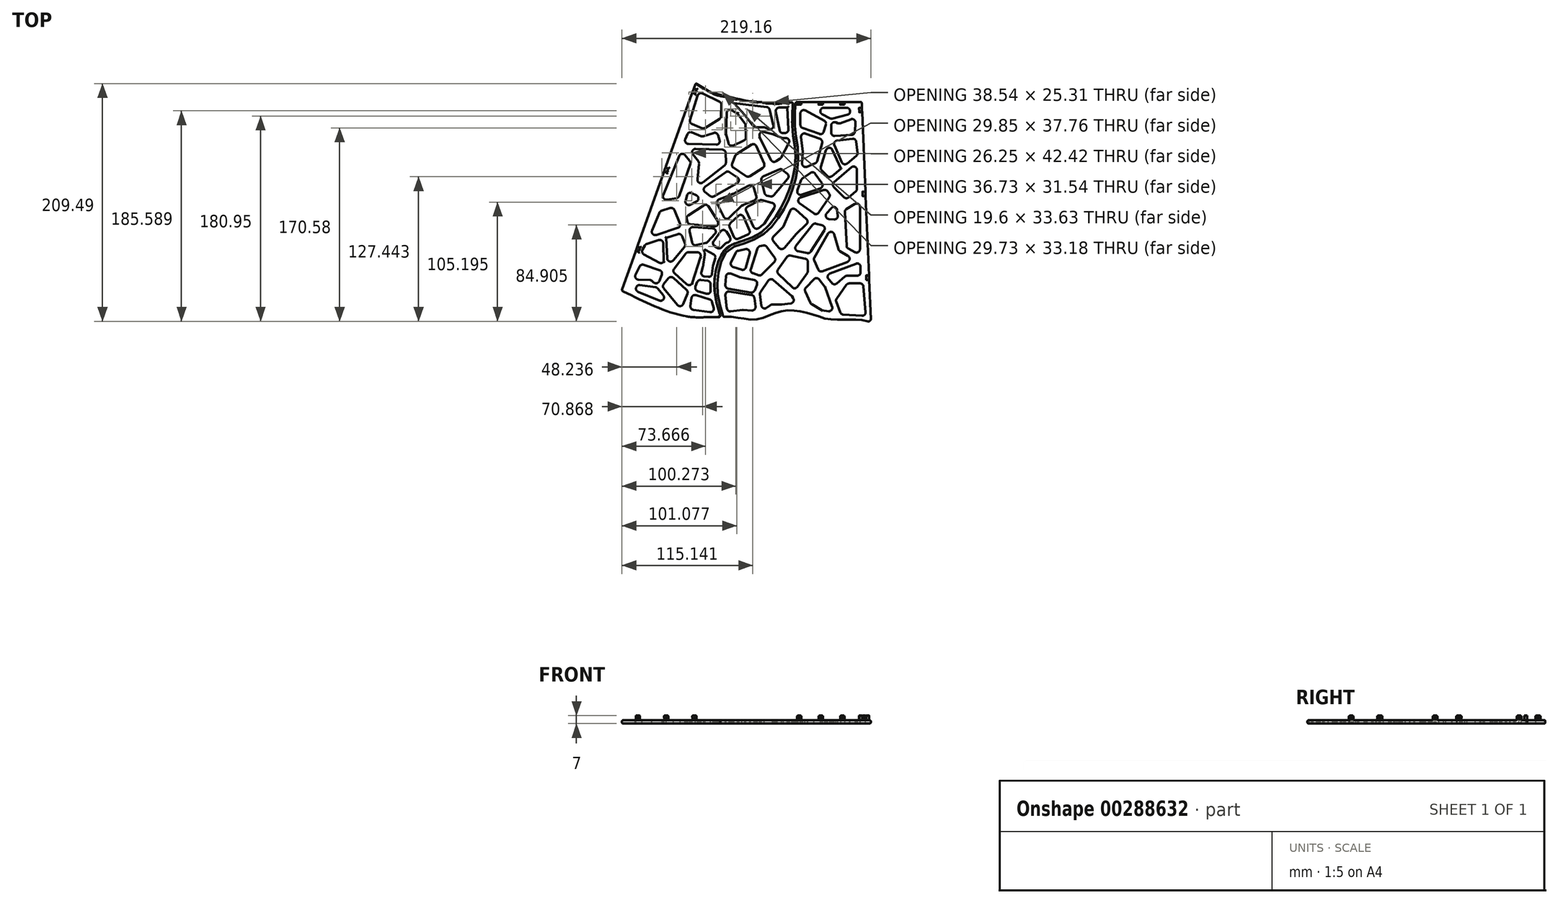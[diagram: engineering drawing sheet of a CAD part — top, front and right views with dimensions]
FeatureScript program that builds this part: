
annotation { "Feature Type Name" : "Feature", "Feature Type Description" : "" }
export const myFeature = defineFeature(function(context is Context, id is Id, definition is map)
    precondition{}
    {
        {
            var Q0;
            Q0=qCreatedBy(makeId("Top.planeOp"),FACE);
            var sketch = newSketch(context, id + "F0", { "sketchPlane" : qUnion([Q0])});
            skPoint(sketch, "E0", {"position": v(69.28, -152.32) * mm});
            skLineSegment(sketch, "E1", {"start": v(30.8, 159.98) * mm, "end": v(38.85, -31.37) * mm});
            skLineSegment(sketch, "E2", {"start": v(30.8, 159.98) * mm, "end": v(-25.68, 159.98) * mm});
            skFitSpline(sketch, "E3", {"points": [v(-27.61, 159.98) * mm, v(-27.61, 133.72) * mm, v(-25.44, 118.63) * mm, v(-27.61, 91.65) * mm, v(-45.45, 53.52) * mm, v(-66.8, 37.33) * mm, v(-86.1, 29.91) * mm, v(-94.25, 14.34) * mm, v(-96.1, -7.92) * mm, v(-91.06, -29.4) * mm], "startDerivative": vector(-8.83, -245.35) * mm, "endDerivative": vector(61.47, -198.5) * mm});
            skFitSpline(sketch, "E4", {"points": [v(-91.06, -29.4) * mm, v(-84.58, -29.4) * mm, v(-69.1, -31.56) * mm, v(-59.54, -31.3) * mm, v(-44.2, -25.79) * mm, v(-29.25, -23.82) * mm, v(-6.17, -29.4) * mm, v(0, -31.34) * mm, v(13.8, -31.87) * mm, v(29.02, -32.13) * mm, v(38.96, -34) * mm], "startDerivative": vector(78.08, 4.89) * mm, "endDerivative": vector(105.84, -25.4) * mm});
            skArc(sketch, "E5.filletArc", {"start": v(-25.68, 159.98) * mm, "mid": v(-27.07, 159.41) * mm, "end": v(-27.68, 158.05) * mm});
            skArc(sketch, "E6.filletArc", {"start": v(-91.52, -27.9) * mm, "mid": v(-90.76, -28.95) * mm, "end": v(-89.52, -29.31) * mm});
            skArc(sketch, "E7.filletArc", {"start": v(36.4, -33.4) * mm, "mid": v(38.13, -32.99) * mm, "end": v(38.85, -31.37) * mm});
            skSolve(sketch);
        }
        {
            var Q0;
            Q0=qCreatedBy(makeId("Top.planeOp"),FACE);
            var sketch = newSketch(context, id + "F1", { "sketchPlane" : qUnion([Q0])});
            skLineSegment(sketch, "E8", {"start": v(-180.19, -4.8) * mm, "end": v(-115.37, 176.62) * mm});
            skFitSpline(sketch, "E9", {"points": [v(-115.37, 176.62) * mm, v(-102.14, 168.68) * mm, v(-86.7, 164.7) * mm, v(-68.18, 160.74) * mm, v(-43.92, 159.41) * mm, v(-29.99, 159.68) * mm], "startDerivative": vector(67.95, -48.1) * mm, "endDerivative": vector(71.48, 2.17) * mm});
            skFitSpline(sketch, "E10", {"points": [v(-29.99, 159.68) * mm, v(-29.99, 155.4) * mm, v(-30.37, 146.31) * mm, v(-29.99, 133.5) * mm, v(-27.85, 118.29) * mm, v(-29.99, 92.6) * mm, v(-47.22, 55.66) * mm, v(-67.43, 39.69) * mm, v(-87.18, 32) * mm, v(-96.99, 14.57) * mm, v(-98.7, -7.72) * mm, v(-93.43, -29.61) * mm], "startDerivative": vector(1.57, -90.12) * mm, "endDerivative": vector(67.23, -218) * mm});
            skFitSpline(sketch, "E11", {"points": [v(-93.43, -29.61) * mm, v(-102.74, -29.61) * mm, v(-119, -29.61) * mm, v(-146.01, -22.4) * mm, v(-168.33, -12.34) * mm, v(-180.8, -6.52) * mm], "startDerivative": vector(-60.72, 1.3) * mm, "endDerivative": vector(-66.19, 30.38) * mm});
            skArc(sketch, "E12.filletArc", {"start": v(-29.96, 157.62) * mm, "mid": v(-30.57, 159.05) * mm, "end": v(-32.02, 159.62) * mm});
            skArc(sketch, "E13.filletArc", {"start": v(-180.19, -4.8) * mm, "mid": v(-180.14, -6.24) * mm, "end": v(-179.14, -7.28) * mm});
            skArc(sketch, "E14.filletArc", {"start": v(-96.18, -29.56) * mm, "mid": v(-94.56, -28.76) * mm, "end": v(-94.24, -26.98) * mm});
            skSolve(sketch);
        }
        {
            var Q0;
            Q0=qCreatedBy(makeId("Top.planeOp"),FACE);
            var sketch = newSketch(context, id + "F2", { "sketchPlane" : qUnion([Q0])});
            skLineSegment(sketch, "E15", {"start": v(31.1, -28.5) * mm, "end": v(14.46, -27.38) * mm});
            skLineSegment(sketch, "E16", {"start": v(11.84, -25.43) * mm, "end": v(8.42, -16.13) * mm});
            skLineSegment(sketch, "E17", {"start": v(8.8, -13.36) * mm, "end": v(17.36, -1.26) * mm});
            skLineSegment(sketch, "E18", {"start": v(19.81, 0) * mm, "end": v(29.41, 0) * mm});
            skLineSegment(sketch, "E19", {"start": v(32.4, -2.75) * mm, "end": v(34.29, -25.26) * mm});
            skLineSegment(sketch, "E20", {"start": v(-1.48, -3.2) * mm, "end": v(4.8, -20.47) * mm});
            skLineSegment(sketch, "E21", {"start": v(1.64, -24.47) * mm, "end": v(-4.13, -23.8) * mm});
            skLineSegment(sketch, "E22", {"start": v(-4.13, -23.8) * mm, "end": v(-13.29, -18.36) * mm});
            skLineSegment(sketch, "E23", {"start": v(-14.5, -17) * mm, "end": v(-18.9, -7.06) * mm});
            skLineSegment(sketch, "E24", {"start": v(-18.35, -3.78) * mm, "end": v(-11.22, 3.75) * mm});
            skLineSegment(sketch, "E25", {"start": v(-6.66, 3.52) * mm, "end": v(-1.48, -3.2) * mm});
            skLineSegment(sketch, "E26", {"start": v(8.78, -0.04) * mm, "end": v(16.2, 6.12) * mm});
            skLineSegment(sketch, "E27", {"start": v(18.13, 6.81) * mm, "end": v(26.87, 6.81) * mm});
            skLineSegment(sketch, "E28", {"start": v(29.87, 9.81) * mm, "end": v(29.87, 14.59) * mm});
            skLineSegment(sketch, "E29", {"start": v(-25.87, -3) * mm, "end": v(-17.08, 9.38) * mm});
            skLineSegment(sketch, "E30", {"start": v(-16.53, 11.12) * mm, "end": v(-16.53, 18.9) * mm});
            skLineSegment(sketch, "E31", {"start": v(-18.93, 21.83) * mm, "end": v(-32.06, 24.49) * mm});
            skLineSegment(sketch, "E32", {"start": v(-35.1, 23.28) * mm, "end": v(-42.92, 12.26) * mm});
            skLineSegment(sketch, "E33", {"start": v(-42.56, 8.37) * mm, "end": v(-30.4, -3.43) * mm});
            skLineSegment(sketch, "E34", {"start": v(-46.96, 3) * mm, "end": v(-30.58, -11.3) * mm});
            skLineSegment(sketch, "E35", {"start": v(-30.58, -11.3) * mm, "end": v(-29.49, -13) * mm});
            skLineSegment(sketch, "E36", {"start": v(-31.66, -17.6) * mm, "end": v(-39.67, -18.53) * mm});
            skLineSegment(sketch, "E37", {"start": v(-39.67, -18.53) * mm, "end": v(-47.78, -18.53) * mm});
            skLineSegment(sketch, "E38", {"start": v(-49.54, -19.1) * mm, "end": v(-52.82, -21.48) * mm});
            skLineSegment(sketch, "E39", {"start": v(-57.56, -19.44) * mm, "end": v(-58.8, -9.65) * mm});
            skLineSegment(sketch, "E40", {"start": v(-58.3, -7.57) * mm, "end": v(-51.4, 2.44) * mm});
            skLineSegment(sketch, "E41", {"start": v(-84.55, -24.65) * mm, "end": v(-74.24, -23.34) * mm});
            skLineSegment(sketch, "E42", {"start": v(-73.65, -23.32) * mm, "end": v(-65.92, -23.84) * mm});
            skLineSegment(sketch, "E43", {"start": v(-62.74, -20.46) * mm, "end": v(-63.73, -12.76) * mm});
            skLineSegment(sketch, "E44", {"start": v(-63.4, -6.1) * mm, "end": v(-61.43, -1.08) * mm});
            skLineSegment(sketch, "E45", {"start": v(-63.63, 2.95) * mm, "end": v(-76.87, 5.63) * mm});
            skLineSegment(sketch, "E46", {"start": v(-77.37, 5.78) * mm, "end": v(-84.68, 8.66) * mm});
            skLineSegment(sketch, "E47", {"start": v(-88.77, 6.07) * mm, "end": v(-89.28, -1.4) * mm});
            skLineSegment(sketch, "E48", {"start": v(-89.2, -10.44) * mm, "end": v(-87.9, -22) * mm});
            skLineSegment(sketch, "E49", {"start": v(-80.06, 27.24) * mm, "end": v(-84.2, 18.7) * mm});
            skLineSegment(sketch, "E50", {"start": v(-82.43, 14.54) * mm, "end": v(-74.91, 12.12) * mm});
            skLineSegment(sketch, "E51", {"start": v(-56.79, 8.03) * mm, "end": v(-46.16, 18.98) * mm});
            skLineSegment(sketch, "E52", {"start": v(-45.89, 22.83) * mm, "end": v(-52.69, 32.18) * mm});
            skLineSegment(sketch, "E53", {"start": v(-55.7, 33.36) * mm, "end": v(-58.78, 32.74) * mm});
            skLineSegment(sketch, "E54", {"start": v(-47, 37.37) * mm, "end": v(-41.99, 31.34) * mm});
            skLineSegment(sketch, "E55", {"start": v(-37.39, 31.32) * mm, "end": v(-26.9, 43.75) * mm});
            skLineSegment(sketch, "E56", {"start": v(-26.9, 43.75) * mm, "end": v(-17.78, 52.23) * mm});
            skLineSegment(sketch, "E57", {"start": v(-17.84, 56.69) * mm, "end": v(-27.46, 65.12) * mm});
            skLineSegment(sketch, "E58", {"start": v(-32.2, 64.04) * mm, "end": v(-38.22, 49.87) * mm});
            skLineSegment(sketch, "E59", {"start": v(-38.22, 49.87) * mm, "end": v(-46.8, 41.42) * mm});
            skLineSegment(sketch, "E60", {"start": v(15.95, 62.82) * mm, "end": v(17.52, 33.04) * mm});
            skLineSegment(sketch, "E61", {"start": v(19.15, 30.53) * mm, "end": v(24.94, 27.57) * mm});
            skLineSegment(sketch, "E62", {"start": v(29.3, 30.24) * mm, "end": v(29.3, 49.62) * mm});
            skLineSegment(sketch, "E63", {"start": v(29.3, 49.62) * mm, "end": v(29.3, 67.45) * mm});
            skLineSegment(sketch, "E64", {"start": v(24.75, 70.01) * mm, "end": v(17.39, 65.55) * mm});
            skLineSegment(sketch, "E65", {"start": v(-23.8, 70.53) * mm, "end": v(-11.29, 61.65) * mm});
            skLineSegment(sketch, "E66", {"start": v(-7.08, 62.4) * mm, "end": v(2.16, 75.8) * mm});
            skLineSegment(sketch, "E67", {"start": v(2.15, 79.23) * mm, "end": v(0.82, 81.12) * mm});
            skLineSegment(sketch, "E68", {"start": v(-14.33, 97.44) * mm, "end": v(-21.45, 92.43) * mm});
            skLineSegment(sketch, "E69", {"start": v(-22.54, 91) * mm, "end": v(-25.8, 82.09) * mm});
            skLineSegment(sketch, "E70", {"start": v(4, 66.34) * mm, "end": v(-0.04, 61.73) * mm});
            skLineSegment(sketch, "E71", {"start": v(2.01, 56.76) * mm, "end": v(6.66, 56.45) * mm});
            skLineSegment(sketch, "E72", {"start": v(9.84, 59.8) * mm, "end": v(9.23, 64.73) * mm});
            skLineSegment(sketch, "E73", {"start": v(6.25, 85.01) * mm, "end": v(15.14, 75.99) * mm});
            skLineSegment(sketch, "E74", {"start": v(19.19, 75.79) * mm, "end": v(25.57, 81.08) * mm});
            skLineSegment(sketch, "E75", {"start": v(26.65, 83.4) * mm, "end": v(26.65, 100.03) * mm});
            skLineSegment(sketch, "E76", {"start": v(21.71, 102.33) * mm, "end": v(6.44, 89.4) * mm});
            skLineSegment(sketch, "E77", {"start": v(-4.47, 99.7) * mm, "end": v(0.44, 94.73) * mm});
            skLineSegment(sketch, "E78", {"start": v(4.5, 94.53) * mm, "end": v(12.58, 101.24) * mm});
            skLineSegment(sketch, "E79", {"start": v(27.22, 115.21) * mm, "end": v(25.98, 124.95) * mm});
            skLineSegment(sketch, "E80", {"start": v(22.62, 127.54) * mm, "end": v(9.09, 125.81) * mm});
            skLineSegment(sketch, "E81", {"start": v(-0.62, 117.4) * mm, "end": v(-5.2, 102.7) * mm});
            skLineSegment(sketch, "E82", {"start": v(-22.57, 128.81) * mm, "end": v(-20.98, 116.36) * mm});
            skLineSegment(sketch, "E83", {"start": v(-20.96, 115.77) * mm, "end": v(-21.63, 105.8) * mm});
            skLineSegment(sketch, "E84", {"start": v(-17.5, 102.83) * mm, "end": v(-10.17, 105.86) * mm});
            skLineSegment(sketch, "E85", {"start": v(-8.42, 107.85) * mm, "end": v(-4.07, 123.93) * mm});
            skLineSegment(sketch, "E86", {"start": v(-5.97, 127.54) * mm, "end": v(-18.6, 132.02) * mm});
            skLineSegment(sketch, "E87", {"start": v(-23.2, 149.78) * mm, "end": v(-23.2, 139.85) * mm});
            skLineSegment(sketch, "E88", {"start": v(-21.2, 137.02) * mm, "end": v(-6.46, 131.76) * mm});
            skLineSegment(sketch, "E89", {"start": v(-2.58, 133.72) * mm, "end": v(-0.7, 139.93) * mm});
            skLineSegment(sketch, "E90", {"start": v(-2.15, 143.44) * mm, "end": v(-18.77, 152.42) * mm});
            skLineSegment(sketch, "E91", {"start": v(-4.02, 149.16) * mm, "end": v(2.88, 145.52) * mm});
            skLineSegment(sketch, "E92", {"start": v(5, 145.26) * mm, "end": v(18.36, 148.6) * mm});
            skLineSegment(sketch, "E93", {"start": v(20.61, 151.9) * mm, "end": v(20.57, 152.2) * mm});
            skLineSegment(sketch, "E94", {"start": v(17.6, 154.81) * mm, "end": v(-2.62, 154.81) * mm});
            skLineSegment(sketch, "E95", {"start": v(3.97, 139.12) * mm, "end": v(3.97, 132.96) * mm});
            skLineSegment(sketch, "E96", {"start": v(7.16, 129.96) * mm, "end": v(22.02, 130.9) * mm});
            skLineSegment(sketch, "E97", {"start": v(24.83, 133.69) * mm, "end": v(25.37, 141.7) * mm});
            skLineSegment(sketch, "E98", {"start": v(21.35, 144.72) * mm, "end": v(11.84, 141.26) * mm});
            skLineSegment(sketch, "E99", {"start": v(9.74, 141.27) * mm, "end": v(8.05, 141.92) * mm});
            skLineSegment(sketch, "E100", {"start": v(4.56, 0.35) * mm, "end": v(1.57, 3.94) * mm});
            skLineSegment(sketch, "E101", {"start": v(2.81, 8.67) * mm, "end": v(25.8, 17.4) * mm});
            skLineSegment(sketch, "E102", {"start": v(1.16, 43.91) * mm, "end": v(-10.86, 22.74) * mm});
            skLineSegment(sketch, "E103", {"start": v(-11, 20.04) * mm, "end": v(-7.57, 12.33) * mm});
            skLineSegment(sketch, "E104", {"start": v(-3.77, 10.74) * mm, "end": v(18.23, 19) * mm});
            skLineSegment(sketch, "E105", {"start": v(18.67, 24.41) * mm, "end": v(11.7, 28.42) * mm});
            skLineSegment(sketch, "E106", {"start": v(10.31, 30.2) * mm, "end": v(6.65, 43.24) * mm});
            skLineSegment(sketch, "E107", {"start": v(-12.4, 51.63) * mm, "end": v(-27.02, 33.16) * mm});
            skLineSegment(sketch, "E108", {"start": v(-25.26, 28.36) * mm, "end": v(-17.12, 26.7) * mm});
            skLineSegment(sketch, "E109", {"start": v(-13.99, 28.05) * mm, "end": v(-2.17, 46.73) * mm});
            skLineSegment(sketch, "E110", {"start": v(-3.93, 51.23) * mm, "end": v(-9.27, 52.67) * mm});
            skLineSegment(sketch, "E111", {"start": v(4.97, 117.77) * mm, "end": v(12.58, 101.24) * mm});
            skPoint(sketch, "E112.endSnap0", {"position": v(14.9, 103.17) * mm});
            skLineSegment(sketch, "E113.trimOffspring", {"start": v(17.96, 105.7) * mm, "end": v(26.17, 112.52) * mm});
            skLineSegment(sketch, "E114", {"start": v(-22.02, 78.21) * mm, "end": v(-5.71, 83.71) * mm});
            skLineSegment(sketch, "E115", {"start": v(-22.97, 75.84) * mm, "end": v(-2.53, 82.25) * mm});
            skLineSegment(sketch, "E116.trimOffspring", {"start": v(-4.22, 88.28) * mm, "end": v(-10.15, 96.71) * mm});
            skLineSegment(sketch, "E117", {"start": v(-71.1, 14.2) * mm, "end": v(-67.85, 26.5) * mm});
            skLineSegment(sketch, "E118", {"start": v(-66.86, 12.67) * mm, "end": v(-61.04, 30.72) * mm});
            skLineSegment(sketch, "E119", {"start": v(-66.7, -7.97) * mm, "end": v(-86.79, -4.56) * mm});
            skLineSegment(sketch, "E120", {"start": v(-85.75, -7.14) * mm, "end": v(-66.24, -10.17) * mm});
            skLineSegment(sketch, "E121.trimOffspring", {"start": v(-64.92, 8.9) * mm, "end": v(-59.86, 7.27) * mm});
            skLineSegment(sketch, "E122.trimOffspring", {"start": v(-71.34, 30.2) * mm, "end": v(-77.96, 28.87) * mm});
            skPoint(sketch, "E123.visualSharp", {"position": v(-23.2, 154.81) * mm});
            skArc(sketch, "E123.filletArc", {"start": v(-18.77, 152.42) * mm, "mid": v(-21.73, 152.36) * mm, "end": v(-23.2, 149.78) * mm});
            skPoint(sketch, "E124.visualSharp", {"position": v(-14.73, 154.81) * mm});
            skArc(sketch, "E124.filletArc", {"start": v(-2.62, 154.81) * mm, "mid": v(-5.53, 152.53) * mm, "end": v(-4.02, 149.16) * mm});
            skPoint(sketch, "E125.visualSharp", {"position": v(20.24, 154.81) * mm});
            skArc(sketch, "E125.filletArc", {"start": v(20.57, 152.2) * mm, "mid": v(19.58, 154.06) * mm, "end": v(17.6, 154.81) * mm});
            skPoint(sketch, "E126.visualSharp", {"position": v(20.95, 149.25) * mm});
            skArc(sketch, "E126.filletArc", {"start": v(18.36, 148.6) * mm, "mid": v(20.11, 149.82) * mm, "end": v(20.61, 151.9) * mm});
            skPoint(sketch, "E127.visualSharp", {"position": v(3.9, 144.98) * mm});
            skArc(sketch, "E127.filletArc", {"start": v(2.88, 145.52) * mm, "mid": v(3.92, 145.2) * mm, "end": v(5, 145.26) * mm});
            skPoint(sketch, "E128.visualSharp", {"position": v(3.97, 143.48) * mm});
            skArc(sketch, "E128.filletArc", {"start": v(8.05, 141.92) * mm, "mid": v(5.27, 141.6) * mm, "end": v(3.97, 139.12) * mm});
            skPoint(sketch, "E129.visualSharp", {"position": v(25.68, 146.3) * mm});
            skArc(sketch, "E129.filletArc", {"start": v(25.37, 141.7) * mm, "mid": v(24.18, 144.3) * mm, "end": v(21.35, 144.72) * mm});
            skPoint(sketch, "E130.visualSharp", {"position": v(10.78, 140.87) * mm});
            skArc(sketch, "E130.filletArc", {"start": v(9.74, 141.27) * mm, "mid": v(10.79, 141.07) * mm, "end": v(11.84, 141.26) * mm});
            skPoint(sketch, "E131.visualSharp", {"position": v(3.97, 129.76) * mm});
            skArc(sketch, "E131.filletArc", {"start": v(3.97, 132.96) * mm, "mid": v(4.92, 130.77) * mm, "end": v(7.16, 129.96) * mm});
            skPoint(sketch, "E132.visualSharp", {"position": v(24.65, 131.06) * mm});
            skArc(sketch, "E132.filletArc", {"start": v(22.02, 130.9) * mm, "mid": v(23.95, 131.76) * mm, "end": v(24.83, 133.69) * mm});
            skPoint(sketch, "E133.visualSharp", {"position": v(25.6, 127.92) * mm});
            skArc(sketch, "E133.filletArc", {"start": v(25.98, 124.95) * mm, "mid": v(24.84, 126.94) * mm, "end": v(22.62, 127.54) * mm});
            skPoint(sketch, "E134.visualSharp", {"position": v(5.1, 125.3) * mm});
            skArc(sketch, "E134.filletArc", {"start": v(9.09, 125.81) * mm, "mid": v(6.86, 124.3) * mm, "end": v(6.73, 121.62) * mm});
            skPoint(sketch, "E135.visualSharp", {"position": v(27.43, 113.58) * mm});
            skArc(sketch, "E135.filletArc", {"start": v(26.17, 112.52) * mm, "mid": v(27.04, 113.73) * mm, "end": v(27.22, 115.21) * mm});
            skPoint(sketch, "E136.visualSharp", {"position": v(26.65, 106.5) * mm});
            skArc(sketch, "E136.filletArc", {"start": v(26.65, 100.03) * mm, "mid": v(24.91, 102.76) * mm, "end": v(21.71, 102.33) * mm});
            skPoint(sketch, "E137.visualSharp", {"position": v(17.07, 74.02) * mm});
            skArc(sketch, "E137.filletArc", {"start": v(15.14, 75.99) * mm, "mid": v(17.12, 75.1) * mm, "end": v(19.19, 75.79) * mm});
            skPoint(sketch, "E138.visualSharp", {"position": v(26.65, 81.98) * mm});
            skArc(sketch, "E138.filletArc", {"start": v(25.57, 81.08) * mm, "mid": v(26.37, 82.12) * mm, "end": v(26.65, 83.4) * mm});
            skPoint(sketch, "E139.visualSharp", {"position": v(3.97, 87.32) * mm});
            skArc(sketch, "E139.filletArc", {"start": v(6.44, 89.4) * mm, "mid": v(5.39, 87.25) * mm, "end": v(6.25, 85.01) * mm});
            skPoint(sketch, "E140.visualSharp", {"position": v(2.37, 92.76) * mm});
            skArc(sketch, "E140.filletArc", {"start": v(0.44, 94.73) * mm, "mid": v(2.43, 93.84) * mm, "end": v(4.5, 94.53) * mm});
            skPoint(sketch, "E141.visualSharp", {"position": v(-5.73, 100.99) * mm});
            skArc(sketch, "E141.filletArc", {"start": v(-5.2, 102.7) * mm, "mid": v(-5.25, 101.1) * mm, "end": v(-4.47, 99.7) * mm});
            skPoint(sketch, "E142.visualSharp", {"position": v(-3.35, 126.6) * mm});
            skArc(sketch, "E142.filletArc", {"start": v(-4.07, 123.93) * mm, "mid": v(-4.31, 126.1) * mm, "end": v(-5.97, 127.54) * mm});
            skPoint(sketch, "E143.visualSharp", {"position": v(-8.8, 106.42) * mm});
            skArc(sketch, "E143.filletArc", {"start": v(-10.17, 105.86) * mm, "mid": v(-9.06, 106.65) * mm, "end": v(-8.42, 107.85) * mm});
            skPoint(sketch, "E144.visualSharp", {"position": v(-23.2, 133.66) * mm});
            skArc(sketch, "E144.filletArc", {"start": v(-18.6, 132.02) * mm, "mid": v(-21.48, 131.53) * mm, "end": v(-22.57, 128.81) * mm});
            skPoint(sketch, "E145.visualSharp", {"position": v(-21.96, 100.99) * mm});
            skArc(sketch, "E145.filletArc", {"start": v(-21.63, 105.8) * mm, "mid": v(-20.4, 103.17) * mm, "end": v(-17.5, 102.83) * mm});
            skPoint(sketch, "E146.visualSharp", {"position": v(-20.94, 116.07) * mm});
            skArc(sketch, "E146.filletArc", {"start": v(-20.96, 115.77) * mm, "mid": v(-20.96, 116.06) * mm, "end": v(-20.98, 116.36) * mm});
            skPoint(sketch, "E147.visualSharp", {"position": v(-11.87, 99.17) * mm});
            skArc(sketch, "E147.filletArc", {"start": v(-10.15, 96.71) * mm, "mid": v(-12.08, 97.94) * mm, "end": v(-14.33, 97.44) * mm});
            skPoint(sketch, "E148.visualSharp", {"position": v(-27.94, 76.22) * mm});
            skArc(sketch, "E148.filletArc", {"start": v(-25.8, 82.09) * mm, "mid": v(-25.13, 78.96) * mm, "end": v(-22.02, 78.21) * mm});
            skPoint(sketch, "E149.visualSharp", {"position": v(-1.91, 85) * mm});
            skArc(sketch, "E149.filletArc", {"start": v(-5.71, 83.71) * mm, "mid": v(-3.82, 85.62) * mm, "end": v(-4.22, 88.28) * mm});
            skPoint(sketch, "E150.visualSharp", {"position": v(-22.22, 91.9) * mm});
            skArc(sketch, "E150.filletArc", {"start": v(-21.45, 92.43) * mm, "mid": v(-22.1, 91.8) * mm, "end": v(-22.54, 91) * mm});
            skPoint(sketch, "E151.visualSharp", {"position": v(-0.44, 82.91) * mm});
            skArc(sketch, "E151.filletArc", {"start": v(0.82, 81.12) * mm, "mid": v(-0.67, 82.23) * mm, "end": v(-2.53, 82.25) * mm});
            skPoint(sketch, "E152.visualSharp", {"position": v(3.35, 77.52) * mm});
            skArc(sketch, "E152.filletArc", {"start": v(2.16, 75.8) * mm, "mid": v(2.7, 77.52) * mm, "end": v(2.15, 79.23) * mm});
            skPoint(sketch, "E153.visualSharp", {"position": v(-8.8, 59.89) * mm});
            skArc(sketch, "E153.filletArc", {"start": v(-11.29, 61.65) * mm, "mid": v(-9.03, 61.14) * mm, "end": v(-7.08, 62.4) * mm});
            skPoint(sketch, "E154.visualSharp", {"position": v(-4.05, 57.17) * mm});
            skArc(sketch, "E154.filletArc", {"start": v(-0.04, 61.73) * mm, "mid": v(-0.56, 58.6) * mm, "end": v(2.01, 56.76) * mm});
            skPoint(sketch, "E155.visualSharp", {"position": v(10.28, 56.2) * mm});
            skArc(sketch, "E155.filletArc", {"start": v(6.66, 56.45) * mm, "mid": v(9.04, 57.38) * mm, "end": v(9.84, 59.8) * mm});
            skPoint(sketch, "E156.visualSharp", {"position": v(-28.74, 74.02) * mm});
            skArc(sketch, "E156.filletArc", {"start": v(-22.97, 75.84) * mm, "mid": v(-25.04, 73.44) * mm, "end": v(-23.8, 70.53) * mm});
            skPoint(sketch, "E157.visualSharp", {"position": v(8.41, 71.38) * mm});
            skArc(sketch, "E157.filletArc", {"start": v(9.23, 64.73) * mm, "mid": v(7.14, 67.23) * mm, "end": v(4, 66.34) * mm});
            skPoint(sketch, "E158.visualSharp", {"position": v(15.85, 64.62) * mm});
            skArc(sketch, "E158.filletArc", {"start": v(17.39, 65.55) * mm, "mid": v(16.29, 64.38) * mm, "end": v(15.95, 62.82) * mm});
            skPoint(sketch, "E159.visualSharp", {"position": v(29.3, 72.78) * mm});
            skArc(sketch, "E159.filletArc", {"start": v(29.3, 67.45) * mm, "mid": v(27.78, 70.06) * mm, "end": v(24.75, 70.01) * mm});
            skPoint(sketch, "E160.visualSharp", {"position": v(17.62, 31.32) * mm});
            skArc(sketch, "E160.filletArc", {"start": v(17.52, 33.04) * mm, "mid": v(18, 31.57) * mm, "end": v(19.15, 30.53) * mm});
            skPoint(sketch, "E161.visualSharp", {"position": v(29.3, 25.33) * mm});
            skArc(sketch, "E161.filletArc", {"start": v(24.94, 27.57) * mm, "mid": v(27.87, 27.68) * mm, "end": v(29.3, 30.24) * mm});
            skPoint(sketch, "E162.visualSharp", {"position": v(-1.11, 7.18) * mm});
            skArc(sketch, "E162.filletArc", {"start": v(2.81, 8.67) * mm, "mid": v(0.98, 6.63) * mm, "end": v(1.57, 3.94) * mm});
            skPoint(sketch, "E163.visualSharp", {"position": v(6.48, -1.96) * mm});
            skArc(sketch, "E163.filletArc", {"start": v(4.56, 0.35) * mm, "mid": v(6.6, -0.72) * mm, "end": v(8.78, -0.04) * mm});
            skPoint(sketch, "E164.visualSharp", {"position": v(29.87, 18.93) * mm});
            skArc(sketch, "E164.filletArc", {"start": v(29.87, 14.59) * mm, "mid": v(28.57, 17.06) * mm, "end": v(25.8, 17.4) * mm});
            skPoint(sketch, "E165.visualSharp", {"position": v(17.04, 6.81) * mm});
            skArc(sketch, "E165.filletArc", {"start": v(18.13, 6.81) * mm, "mid": v(17.1, 6.64) * mm, "end": v(16.2, 6.12) * mm});
            skPoint(sketch, "E166.visualSharp", {"position": v(29.87, 6.81) * mm});
            skArc(sketch, "E166.filletArc", {"start": v(26.87, 6.81) * mm, "mid": v(28.99, 7.7) * mm, "end": v(29.87, 9.81) * mm});
            skPoint(sketch, "E167.visualSharp", {"position": v(24.18, 21.24) * mm});
            skArc(sketch, "E167.filletArc", {"start": v(18.23, 19) * mm, "mid": v(20.16, 21.57) * mm, "end": v(18.67, 24.41) * mm});
            skPoint(sketch, "E168.visualSharp", {"position": v(4.7, 50.17) * mm});
            skArc(sketch, "E168.filletArc", {"start": v(6.65, 43.24) * mm, "mid": v(4.13, 45.4) * mm, "end": v(1.16, 43.91) * mm});
            skPoint(sketch, "E169.visualSharp", {"position": v(-11.61, 21.42) * mm});
            skArc(sketch, "E169.filletArc", {"start": v(-10.86, 22.74) * mm, "mid": v(-11.25, 21.4) * mm, "end": v(-11, 20.04) * mm});
            skPoint(sketch, "E170.visualSharp", {"position": v(10.64, 29.03) * mm});
            skArc(sketch, "E170.filletArc", {"start": v(10.31, 30.2) * mm, "mid": v(10.83, 29.18) * mm, "end": v(11.7, 28.42) * mm});
            skPoint(sketch, "E171.visualSharp", {"position": v(-8.8, 6.3) * mm});
            skArc(sketch, "E171.filletArc", {"start": v(-6.66, 3.52) * mm, "mid": v(-8.89, 4.69) * mm, "end": v(-11.22, 3.75) * mm});
            skPoint(sketch, "E172.visualSharp", {"position": v(6.48, -25.04) * mm});
            skArc(sketch, "E172.filletArc", {"start": v(1.64, -24.47) * mm, "mid": v(4.34, -23.35) * mm, "end": v(4.8, -20.47) * mm});
            skPoint(sketch, "E173.visualSharp", {"position": v(-19.72, -5.24) * mm});
            skArc(sketch, "E173.filletArc", {"start": v(-18.35, -3.78) * mm, "mid": v(-19.13, -5.34) * mm, "end": v(-18.9, -7.06) * mm});
            skPoint(sketch, "E174.visualSharp", {"position": v(7.88, -14.64) * mm});
            skArc(sketch, "E174.filletArc", {"start": v(8.8, -13.36) * mm, "mid": v(8.26, -14.7) * mm, "end": v(8.42, -16.13) * mm});
            skPoint(sketch, "E175.visualSharp", {"position": v(18.26, 0) * mm});
            skArc(sketch, "E175.filletArc", {"start": v(19.81, 0) * mm, "mid": v(18.43, -0.33) * mm, "end": v(17.36, -1.26) * mm});
            skPoint(sketch, "E176.visualSharp", {"position": v(32.17, 0) * mm});
            skArc(sketch, "E176.filletArc", {"start": v(32.4, -2.75) * mm, "mid": v(31.44, -0.8) * mm, "end": v(29.41, 0) * mm});
            skPoint(sketch, "E177.visualSharp", {"position": v(34.58, -28.74) * mm});
            skArc(sketch, "E177.filletArc", {"start": v(31.1, -28.5) * mm, "mid": v(33.44, -27.61) * mm, "end": v(34.29, -25.26) * mm});
            skPoint(sketch, "E178.visualSharp", {"position": v(12.51, -27.25) * mm});
            skArc(sketch, "E178.filletArc", {"start": v(11.84, -25.43) * mm, "mid": v(12.86, -26.8) * mm, "end": v(14.46, -27.38) * mm});
            skPoint(sketch, "E179.visualSharp", {"position": v(-26.87, -17.04) * mm});
            skArc(sketch, "E179.filletArc", {"start": v(-31.66, -17.6) * mm, "mid": v(-29.3, -15.9) * mm, "end": v(-29.49, -13) * mm});
            skPoint(sketch, "E180.visualSharp", {"position": v(-58.95, -8.51) * mm});
            skArc(sketch, "E180.filletArc", {"start": v(-58.3, -7.57) * mm, "mid": v(-58.75, -8.56) * mm, "end": v(-58.8, -9.65) * mm});
            skPoint(sketch, "E181.visualSharp", {"position": v(-49.5, 5.2) * mm});
            skArc(sketch, "E181.filletArc", {"start": v(-46.96, 3) * mm, "mid": v(-49.3, 3.71) * mm, "end": v(-51.4, 2.44) * mm});
            skPoint(sketch, "E182.visualSharp", {"position": v(-48.75, -18.53) * mm});
            skArc(sketch, "E182.filletArc", {"start": v(-47.78, -18.53) * mm, "mid": v(-48.7, -18.68) * mm, "end": v(-49.54, -19.1) * mm});
            skPoint(sketch, "E183.visualSharp", {"position": v(-56.91, -24.46) * mm});
            skArc(sketch, "E183.filletArc", {"start": v(-57.56, -19.44) * mm, "mid": v(-55.77, -21.81) * mm, "end": v(-52.82, -21.48) * mm});
            skPoint(sketch, "E184.visualSharp", {"position": v(-62.28, -24.08) * mm});
            skArc(sketch, "E184.filletArc", {"start": v(-65.92, -23.84) * mm, "mid": v(-63.53, -22.9) * mm, "end": v(-62.74, -20.46) * mm});
            skPoint(sketch, "E185.visualSharp", {"position": v(-87.57, -25.04) * mm});
            skArc(sketch, "E185.filletArc", {"start": v(-87.9, -22) * mm, "mid": v(-86.78, -24.04) * mm, "end": v(-84.55, -24.65) * mm});
            skPoint(sketch, "E186.visualSharp", {"position": v(-64.01, -10.52) * mm});
            skArc(sketch, "E186.filletArc", {"start": v(-63.73, -12.76) * mm, "mid": v(-64.55, -11.04) * mm, "end": v(-66.24, -10.17) * mm});
            skPoint(sketch, "E187.visualSharp", {"position": v(-64.28, -8.38) * mm});
            skArc(sketch, "E187.filletArc", {"start": v(-66.7, -7.97) * mm, "mid": v(-64.71, -7.63) * mm, "end": v(-63.4, -6.1) * mm});
            skPoint(sketch, "E188.visualSharp", {"position": v(-89.46, -4.1) * mm});
            skArc(sketch, "E188.filletArc", {"start": v(-89.28, -1.4) * mm, "mid": v(-88.64, -3.46) * mm, "end": v(-86.79, -4.56) * mm});
            skPoint(sketch, "E189.visualSharp", {"position": v(-85.72, 15.6) * mm});
            skArc(sketch, "E189.filletArc", {"start": v(-84.2, 18.7) * mm, "mid": v(-84.27, 16.22) * mm, "end": v(-82.43, 14.54) * mm});
            skPoint(sketch, "E190.visualSharp", {"position": v(-66.62, 31.16) * mm});
            skArc(sketch, "E190.filletArc", {"start": v(-67.85, 26.5) * mm, "mid": v(-68.56, 29.32) * mm, "end": v(-71.34, 30.2) * mm});
            skPoint(sketch, "E191.visualSharp", {"position": v(-88.5, 10.16) * mm});
            skArc(sketch, "E191.filletArc", {"start": v(-84.68, 8.66) * mm, "mid": v(-87.39, 8.4) * mm, "end": v(-88.77, 6.07) * mm});
            skPoint(sketch, "E192.visualSharp", {"position": v(-71.9, 11.15) * mm});
            skArc(sketch, "E192.filletArc", {"start": v(-74.91, 12.12) * mm, "mid": v(-72.56, 12.34) * mm, "end": v(-71.1, 14.2) * mm});
            skPoint(sketch, "E193.visualSharp", {"position": v(-79.41, 28.58) * mm});
            skArc(sketch, "E193.filletArc", {"start": v(-77.96, 28.87) * mm, "mid": v(-79.2, 28.3) * mm, "end": v(-80.06, 27.24) * mm});
            skPoint(sketch, "E194.visualSharp", {"position": v(-60.5, 32.4) * mm});
            skArc(sketch, "E194.filletArc", {"start": v(-58.78, 32.74) * mm, "mid": v(-60.19, 32.04) * mm, "end": v(-61.04, 30.72) * mm});
            skPoint(sketch, "E195.visualSharp", {"position": v(-53.82, 33.74) * mm});
            skArc(sketch, "E195.filletArc", {"start": v(-52.69, 32.18) * mm, "mid": v(-54.03, 33.21) * mm, "end": v(-55.7, 33.36) * mm});
            skPoint(sketch, "E196.visualSharp", {"position": v(-44.4, 20.8) * mm});
            skArc(sketch, "E196.filletArc", {"start": v(-46.16, 18.98) * mm, "mid": v(-45.32, 20.86) * mm, "end": v(-45.89, 22.83) * mm});
            skPoint(sketch, "E197.visualSharp", {"position": v(-67.78, 9.82) * mm});
            skArc(sketch, "E197.filletArc", {"start": v(-66.86, 12.67) * mm, "mid": v(-66.67, 10.39) * mm, "end": v(-64.92, 8.9) * mm});
            skPoint(sketch, "E198.visualSharp", {"position": v(-58.09, 6.7) * mm});
            skArc(sketch, "E198.filletArc", {"start": v(-59.86, 7.27) * mm, "mid": v(-58.22, 7.21) * mm, "end": v(-56.79, 8.03) * mm});
            skPoint(sketch, "E199.visualSharp", {"position": v(-33.97, 24.88) * mm});
            skArc(sketch, "E199.filletArc", {"start": v(-32.06, 24.49) * mm, "mid": v(-33.76, 24.34) * mm, "end": v(-35.1, 23.28) * mm});
            skPoint(sketch, "E200.visualSharp", {"position": v(-16.53, 21.35) * mm});
            skArc(sketch, "E200.filletArc", {"start": v(-16.53, 18.9) * mm, "mid": v(-17.2, 20.8) * mm, "end": v(-18.93, 21.83) * mm});
            skPoint(sketch, "E201.visualSharp", {"position": v(-16.53, 10.16) * mm});
            skArc(sketch, "E201.filletArc", {"start": v(-17.08, 9.38) * mm, "mid": v(-16.67, 10.2) * mm, "end": v(-16.53, 11.12) * mm});
            skPoint(sketch, "E202.visualSharp", {"position": v(-27.9, -5.86) * mm});
            skArc(sketch, "E202.filletArc", {"start": v(-30.4, -3.43) * mm, "mid": v(-28.04, -4.26) * mm, "end": v(-25.87, -3) * mm});
            skPoint(sketch, "E203.visualSharp", {"position": v(-44.4, 10.16) * mm});
            skArc(sketch, "E203.filletArc", {"start": v(-42.92, 12.26) * mm, "mid": v(-43.46, 10.25) * mm, "end": v(-42.56, 8.37) * mm});
            skPoint(sketch, "E204.visualSharp", {"position": v(-39.7, 28.58) * mm});
            skArc(sketch, "E204.filletArc", {"start": v(-41.99, 31.34) * mm, "mid": v(-39.7, 30.25) * mm, "end": v(-37.39, 31.32) * mm});
            skPoint(sketch, "E205.visualSharp", {"position": v(-30.58, 67.86) * mm});
            skArc(sketch, "E205.filletArc", {"start": v(-27.46, 65.12) * mm, "mid": v(-30.1, 65.8) * mm, "end": v(-32.2, 64.04) * mm});
            skPoint(sketch, "E206.visualSharp", {"position": v(-15.34, 54.5) * mm});
            skArc(sketch, "E206.filletArc", {"start": v(-17.78, 52.23) * mm, "mid": v(-16.82, 54.47) * mm, "end": v(-17.84, 56.69) * mm});
            skPoint(sketch, "E207.visualSharp", {"position": v(-48.75, 39.49) * mm});
            skArc(sketch, "E207.filletArc", {"start": v(-46.8, 41.42) * mm, "mid": v(-47.68, 39.43) * mm, "end": v(-47, 37.37) * mm});
            skPoint(sketch, "E208.visualSharp", {"position": v(-30.05, 29.33) * mm});
            skArc(sketch, "E208.filletArc", {"start": v(-27.02, 33.16) * mm, "mid": v(-27.48, 30.27) * mm, "end": v(-25.26, 28.36) * mm});
            skPoint(sketch, "E209.visualSharp", {"position": v(-15.1, 26.3) * mm});
            skArc(sketch, "E209.filletArc", {"start": v(-17.12, 26.7) * mm, "mid": v(-15.34, 26.9) * mm, "end": v(-13.99, 28.05) * mm});
            skPoint(sketch, "E210.visualSharp", {"position": v(0, 50.17) * mm});
            skArc(sketch, "E210.filletArc", {"start": v(-2.17, 46.73) * mm, "mid": v(-1.92, 49.42) * mm, "end": v(-3.93, 51.23) * mm});
            skPoint(sketch, "E211.visualSharp", {"position": v(-11.18, 53.19) * mm});
            skArc(sketch, "E211.filletArc", {"start": v(-9.27, 52.67) * mm, "mid": v(-11, 52.62) * mm, "end": v(-12.4, 51.63) * mm});
            skPoint(sketch, "E212.visualSharp", {"position": v(-6.42, 9.74) * mm});
            skArc(sketch, "E212.filletArc", {"start": v(-7.57, 12.33) * mm, "mid": v(-5.98, 10.78) * mm, "end": v(-3.77, 10.74) * mm});
            skPoint(sketch, "E213.visualSharp", {"position": v(-89.62, -6.54) * mm});
            skArc(sketch, "E213.filletArc", {"start": v(-85.75, -7.14) * mm, "mid": v(-88.28, -7.94) * mm, "end": v(-89.2, -10.44) * mm});
            skPoint(sketch, "E214.visualSharp", {"position": v(-60.13, 2.25) * mm});
            skArc(sketch, "E214.filletArc", {"start": v(-61.43, -1.08) * mm, "mid": v(-61.59, 1.45) * mm, "end": v(-63.63, 2.95) * mm});
            skPoint(sketch, "E215.visualSharp", {"position": v(-77.13, 5.69) * mm});
            skArc(sketch, "E215.filletArc", {"start": v(-77.37, 5.78) * mm, "mid": v(-77.13, 5.7) * mm, "end": v(-76.87, 5.63) * mm});
            skPoint(sketch, "E216.visualSharp", {"position": v(-73.95, -23.3) * mm});
            skArc(sketch, "E216.filletArc", {"start": v(-73.65, -23.32) * mm, "mid": v(-73.95, -23.31) * mm, "end": v(-74.24, -23.34) * mm});
            skPoint(sketch, "E217.visualSharp", {"position": v(-14.1, -17.87) * mm});
            skArc(sketch, "E217.filletArc", {"start": v(-14.5, -17) * mm, "mid": v(-14, -17.77) * mm, "end": v(-13.29, -18.36) * mm});
            skPoint(sketch, "E218.visualSharp", {"position": v(-3.5, 130.7) * mm});
            skArc(sketch, "E218.filletArc", {"start": v(-6.46, 131.76) * mm, "mid": v(-4.1, 131.9) * mm, "end": v(-2.58, 133.72) * mm});
            skPoint(sketch, "E219.visualSharp", {"position": v(-23.2, 137.74) * mm});
            skArc(sketch, "E219.filletArc", {"start": v(-23.2, 139.85) * mm, "mid": v(-22.65, 138.12) * mm, "end": v(-21.2, 137.02) * mm});
            skPoint(sketch, "E220.visualSharp", {"position": v(0, 142.27) * mm});
            skArc(sketch, "E220.filletArc", {"start": v(-0.7, 139.93) * mm, "mid": v(-0.8, 141.94) * mm, "end": v(-2.15, 143.44) * mm});
            skPoint(sketch, "E221.visualSharp", {"position": v(1.7, 124.87) * mm});
            skArc(sketch, "E221.filletArc", {"start": v(4.97, 117.77) * mm, "mid": v(2.05, 119.51) * mm, "end": v(-0.62, 117.4) * mm});
            skLineSegment(sketch, "E222", {"start": v(6.73, 121.62) * mm, "end": v(13.3, 106.8) * mm});
            skArc(sketch, "E223.filletArc", {"start": v(13.3, 106.8) * mm, "mid": v(15.35, 105.1) * mm, "end": v(17.96, 105.7) * mm});
            skSolve(sketch);
        }
        {
            var Q0;
            Q0=qCreatedBy(makeId("Top.planeOp"),FACE);
            var sketch = newSketch(context, id + "F3", { "sketchPlane" : qUnion([Q0])});
            skLineSegment(sketch, "E224", {"start": v(-109.44, 167.42) * mm, "end": v(-94.45, 160.1) * mm});
            skLineSegment(sketch, "E225", {"start": v(-92.77, 157.3) * mm, "end": v(-93.11, 147.4) * mm});
            skLineSegment(sketch, "E226", {"start": v(-94.5, 144.98) * mm, "end": v(-107, 137.02) * mm});
            skLineSegment(sketch, "E227", {"start": v(-109.75, 136.77) * mm, "end": v(-118.64, 140.4) * mm});
            skLineSegment(sketch, "E228", {"start": v(-120.37, 144.07) * mm, "end": v(-113.62, 165.62) * mm});
            skLineSegment(sketch, "E229", {"start": v(-88.82, 131.7) * mm, "end": v(-88.13, 150.06) * mm});
            skLineSegment(sketch, "E230", {"start": v(-83.68, 152.57) * mm, "end": v(-78.6, 149.77) * mm});
            skLineSegment(sketch, "E231", {"start": v(-78.6, 149.77) * mm, "end": v(-72.17, 141.28) * mm});
            skLineSegment(sketch, "E232", {"start": v(-71.56, 139.56) * mm, "end": v(-71.23, 128.7) * mm});
            skLineSegment(sketch, "E233", {"start": v(-72.98, 125.87) * mm, "end": v(-82.43, 121.58) * mm});
            skLineSegment(sketch, "E234", {"start": v(-86.56, 123.52) * mm, "end": v(-88.82, 131.7) * mm});
            skLineSegment(sketch, "E235", {"start": v(-99.52, 132.65) * mm, "end": v(-108.72, 129.74) * mm});
            skLineSegment(sketch, "E236", {"start": v(-110.76, 129.82) * mm, "end": v(-118.85, 133.12) * mm});
            skLineSegment(sketch, "E237", {"start": v(-122.76, 131.48) * mm, "end": v(-124.57, 127.06) * mm});
            skLineSegment(sketch, "E238", {"start": v(-66.31, 122.31) * mm, "end": v(-79.13, 114.16) * mm});
            skLineSegment(sketch, "E239", {"start": v(-80.3, 112.76) * mm, "end": v(-83.23, 105.56) * mm});
            skLineSegment(sketch, "E240", {"start": v(-82.11, 101.93) * mm, "end": v(-70.96, 94.51) * mm});
            skLineSegment(sketch, "E241", {"start": v(-67.69, 94.48) * mm, "end": v(-56.29, 101.74) * mm});
            skLineSegment(sketch, "E242", {"start": v(-55.15, 105.48) * mm, "end": v(-61.95, 120.99) * mm});
            skLineSegment(sketch, "E243", {"start": v(-49.04, 108.8) * mm, "end": v(-58.82, 128.2) * mm});
            skLineSegment(sketch, "E244", {"start": v(-58.82, 128.2) * mm, "end": v(-59.2, 130.2) * mm});
            skLineSegment(sketch, "E245", {"start": v(-55.44, 133.64) * mm, "end": v(-47.68, 131.48) * mm});
            skLineSegment(sketch, "E246", {"start": v(-47.68, 131.48) * mm, "end": v(-39.83, 128.28) * mm});
            skLineSegment(sketch, "E247", {"start": v(-38.65, 128.06) * mm, "end": v(-35.98, 128.1) * mm});
            skLineSegment(sketch, "E248", {"start": v(-33.3, 123.68) * mm, "end": v(-40.06, 111.12) * mm});
            skLineSegment(sketch, "E249", {"start": v(-41.06, 110.03) * mm, "end": v(-44.72, 107.63) * mm});
            skLineSegment(sketch, "E250", {"start": v(-41.85, 100.42) * mm, "end": v(-55.82, 94.3) * mm});
            skLineSegment(sketch, "E251", {"start": v(-57.53, 90.83) * mm, "end": v(-54.76, 79.6) * mm});
            skLineSegment(sketch, "E252", {"start": v(-52.4, 77.38) * mm, "end": v(-49.32, 76.79) * mm});
            skLineSegment(sketch, "E253", {"start": v(-61.99, 76.95) * mm, "end": v(-64.35, 84.42) * mm});
            skLineSegment(sketch, "E254", {"start": v(-68.6, 86.18) * mm, "end": v(-83, 78.62) * mm});
            skLineSegment(sketch, "E255", {"start": v(-83, 78.62) * mm, "end": v(-94.66, 74.21) * mm});
            skLineSegment(sketch, "E256", {"start": v(-96.28, 70.06) * mm, "end": v(-90.55, 58.62) * mm});
            skLineSegment(sketch, "E257", {"start": v(-85.75, 57.83) * mm, "end": v(-74.84, 68.69) * mm});
            skLineSegment(sketch, "E258", {"start": v(-74.84, 68.69) * mm, "end": v(-63.7, 73.28) * mm});
            skLineSegment(sketch, "E259", {"start": v(-129.88, 77.13) * mm, "end": v(-120.1, 105.31) * mm});
            skLineSegment(sketch, "E260", {"start": v(-120.66, 108.25) * mm, "end": v(-124.9, 113.18) * mm});
            skLineSegment(sketch, "E261", {"start": v(-129.95, 112.35) * mm, "end": v(-137.27, 94.4) * mm});
            skLineSegment(sketch, "E262", {"start": v(-137.27, 94.4) * mm, "end": v(-144, 77.9) * mm});
            skLineSegment(sketch, "E263", {"start": v(-140.74, 73.8) * mm, "end": v(-132.24, 75.15) * mm});
            skLineSegment(sketch, "E264", {"start": v(-95.97, 55) * mm, "end": v(-104.22, 67.94) * mm});
            skLineSegment(sketch, "E265", {"start": v(-108.4, 68.84) * mm, "end": v(-122.01, 59.91) * mm});
            skLineSegment(sketch, "E266", {"start": v(-123.3, 56.73) * mm, "end": v(-122.78, 54.48) * mm});
            skLineSegment(sketch, "E267", {"start": v(-114.91, 33.65) * mm, "end": v(-106.43, 35.6) * mm});
            skLineSegment(sketch, "E268", {"start": v(-104.88, 36.5) * mm, "end": v(-98.5, 43.54) * mm});
            skLineSegment(sketch, "E269", {"start": v(-120.15, 69.36) * mm, "end": v(-114.66, 72.1) * mm});
            skLineSegment(sketch, "E270", {"start": v(-114.69, 77.49) * mm, "end": v(-118.88, 79.53) * mm});
            skLineSegment(sketch, "E271", {"start": v(-123.09, 77.62) * mm, "end": v(-124.39, 72.83) * mm});
            skLineSegment(sketch, "E272", {"start": v(-129.27, 52.93) * mm, "end": v(-134.1, 64.64) * mm});
            skLineSegment(sketch, "E273", {"start": v(-137.78, 66.35) * mm, "end": v(-145.68, 63.86) * mm});
            skLineSegment(sketch, "E274", {"start": v(-147.56, 62.13) * mm, "end": v(-153.84, 46.72) * mm});
            skLineSegment(sketch, "E275", {"start": v(-150.13, 42.73) * mm, "end": v(-131.12, 48.93) * mm});
            skLineSegment(sketch, "E276", {"start": v(-124.9, 35.27) * mm, "end": v(-127.56, 41.74) * mm});
            skLineSegment(sketch, "E277", {"start": v(-131.24, 43.45) * mm, "end": v(-141.27, 40.29) * mm});
            skLineSegment(sketch, "E278", {"start": v(-160.25, 33.4) * mm, "end": v(-162.27, 29.65) * mm});
            skLineSegment(sketch, "E279", {"start": v(-161.05, 25.59) * mm, "end": v(-147.44, 18.25) * mm});
            skLineSegment(sketch, "E280", {"start": v(-135.14, 20.33) * mm, "end": v(-125.36, 32.22) * mm});
            skLineSegment(sketch, "E281", {"start": v(-114.01, 27.46) * mm, "end": v(-121.94, 27.43) * mm});
            skLineSegment(sketch, "E282", {"start": v(-124.3, 26.24) * mm, "end": v(-134.4, 13) * mm});
            skLineSegment(sketch, "E283", {"start": v(-134.01, 8.94) * mm, "end": v(-123.2, -0.7) * mm});
            skLineSegment(sketch, "E284", {"start": v(-126.46, -18.16) * mm, "end": v(-122.7, -8.97) * mm});
            skLineSegment(sketch, "E285", {"start": v(-123.49, -5.6) * mm, "end": v(-135.15, 4.84) * mm});
            skLineSegment(sketch, "E286", {"start": v(-139.48, 4.49) * mm, "end": v(-143.56, -0.56) * mm});
            skLineSegment(sketch, "E287", {"start": v(-143.55, -4.35) * mm, "end": v(-131.55, -18.94) * mm});
            skLineSegment(sketch, "E288", {"start": v(-143.98, -10.35) * mm, "end": v(-148.99, -4.38) * mm});
            skLineSegment(sketch, "E289", {"start": v(-150.86, -3.34) * mm, "end": v(-164.42, -1.4) * mm});
            skLineSegment(sketch, "E290", {"start": v(-167.49, -2.95) * mm, "end": v(-167.64, -3.23) * mm});
            skLineSegment(sketch, "E291", {"start": v(-166.13, -7.43) * mm, "end": v(-147.4, -15.06) * mm});
            skLineSegment(sketch, "E292", {"start": v(-147.6, 1.96) * mm, "end": v(-145.26, 7.67) * mm});
            skLineSegment(sketch, "E293", {"start": v(-147.09, 11.65) * mm, "end": v(-161.2, 16.4) * mm});
            skLineSegment(sketch, "E294", {"start": v(-164.85, 14.86) * mm, "end": v(-168.38, 7.65) * mm});
            skLineSegment(sketch, "E295", {"start": v(-165.8, 3.33) * mm, "end": v(-155.68, 2.95) * mm});
            skLineSegment(sketch, "E296", {"start": v(-153.74, 2.14) * mm, "end": v(-152.42, 0.9) * mm});
            skLineSegment(sketch, "E297", {"start": v(-95.76, 130.7) * mm, "end": v(-94.35, 126.23) * mm});
            skLineSegment(sketch, "E298", {"start": v(-97.28, 122.33) * mm, "end": v(-121.86, 122.93) * mm});
            skLineSegment(sketch, "E299", {"start": v(-109.05, 89.07) * mm, "end": v(-89.93, 104.13) * mm});
            skLineSegment(sketch, "E300", {"start": v(-88.78, 106.58) * mm, "end": v(-89.05, 115.02) * mm});
            skLineSegment(sketch, "E301", {"start": v(-91.96, 117.93) * mm, "end": v(-115.45, 118.58) * mm});
            skLineSegment(sketch, "E302", {"start": v(-117.9, 113.73) * mm, "end": v(-112.97, 107.4) * mm});
            skLineSegment(sketch, "E303", {"start": v(-112.35, 105.21) * mm, "end": v(-113.88, 91.76) * mm});
            skLineSegment(sketch, "E304", {"start": v(-99.4, 76.8) * mm, "end": v(-78.9, 88.39) * mm});
            skLineSegment(sketch, "E305", {"start": v(-78.71, 93.5) * mm, "end": v(-85.63, 98.1) * mm});
            skLineSegment(sketch, "E306", {"start": v(-89.04, 98.04) * mm, "end": v(-107.03, 85.2) * mm});
            skLineSegment(sketch, "E307", {"start": v(-107.1, 80.37) * mm, "end": v(-102.7, 77.02) * mm});
            skLineSegment(sketch, "E308", {"start": v(-140.46, 22.1) * mm, "end": v(-141.27, 40.29) * mm});
            skPoint(sketch, "E309.endSnap0", {"position": v(-144.14, 39.38) * mm});
            skLineSegment(sketch, "E310.trimOffspring", {"start": v(-147.93, 38.18) * mm, "end": v(-158.52, 34.84) * mm});
            skLineSegment(sketch, "E311", {"start": v(-100.53, 48.55) * mm, "end": v(-117.7, 49.61) * mm});
            skLineSegment(sketch, "E312", {"start": v(-98.75, 50.4) * mm, "end": v(-120.1, 52.17) * mm});
            skLineSegment(sketch, "E313.trimOffspring", {"start": v(-120.82, 45.95) * mm, "end": v(-118.5, 35.9) * mm});
            skLineSegment(sketch, "E314", {"start": v(-34.27, 92.32) * mm, "end": v(-46.47, 77.8) * mm});
            skLineSegment(sketch, "E315.trimOffspring", {"start": v(-34.64, 96.55) * mm, "end": v(-38.71, 99.97) * mm});
            skPoint(sketch, "E316.visualSharp", {"position": v(-128.36, -22.82) * mm});
            skArc(sketch, "E316.filletArc", {"start": v(-131.55, -18.94) * mm, "mid": v(-128.79, -20) * mm, "end": v(-126.46, -18.16) * mm});
            skPoint(sketch, "E317.visualSharp", {"position": v(-136.2, -19.63) * mm});
            skArc(sketch, "E317.filletArc", {"start": v(-147.4, -15.06) * mm, "mid": v(-143.85, -14.05) * mm, "end": v(-143.98, -10.35) * mm});
            skPoint(sketch, "E318.visualSharp", {"position": v(-169.22, -6.17) * mm});
            skArc(sketch, "E318.filletArc", {"start": v(-167.64, -3.23) * mm, "mid": v(-167.82, -5.66) * mm, "end": v(-166.13, -7.43) * mm});
            skPoint(sketch, "E319.visualSharp", {"position": v(-166.5, -1.1) * mm});
            skArc(sketch, "E319.filletArc", {"start": v(-164.42, -1.4) * mm, "mid": v(-166.2, -1.7) * mm, "end": v(-167.49, -2.95) * mm});
            skPoint(sketch, "E320.visualSharp", {"position": v(-149.73, -3.5) * mm});
            skArc(sketch, "E320.filletArc", {"start": v(-148.99, -4.38) * mm, "mid": v(-149.83, -3.69) * mm, "end": v(-150.86, -3.34) * mm});
            skPoint(sketch, "E321.visualSharp", {"position": v(-149.24, -2.08) * mm});
            skArc(sketch, "E321.filletArc", {"start": v(-152.42, 0.9) * mm, "mid": v(-149.73, 0.16) * mm, "end": v(-147.6, 1.96) * mm});
            skPoint(sketch, "E322.visualSharp", {"position": v(-170.4, 3.5) * mm});
            skArc(sketch, "E322.filletArc", {"start": v(-168.38, 7.65) * mm, "mid": v(-168.25, 4.8) * mm, "end": v(-165.8, 3.33) * mm});
            skPoint(sketch, "E323.visualSharp", {"position": v(-154.56, 2.9) * mm});
            skArc(sketch, "E323.filletArc", {"start": v(-153.74, 2.14) * mm, "mid": v(-154.64, 2.72) * mm, "end": v(-155.68, 2.95) * mm});
            skPoint(sketch, "E324.visualSharp", {"position": v(-144.06, 10.63) * mm});
            skArc(sketch, "E324.filletArc", {"start": v(-145.26, 7.67) * mm, "mid": v(-145.31, 10.05) * mm, "end": v(-147.09, 11.65) * mm});
            skPoint(sketch, "E325.visualSharp", {"position": v(-163.7, 17.23) * mm});
            skArc(sketch, "E325.filletArc", {"start": v(-161.2, 16.4) * mm, "mid": v(-163.31, 16.32) * mm, "end": v(-164.85, 14.86) * mm});
            skPoint(sketch, "E326.visualSharp", {"position": v(-163.7, 27.01) * mm});
            skArc(sketch, "E326.filletArc", {"start": v(-162.27, 29.65) * mm, "mid": v(-162.5, 27.37) * mm, "end": v(-161.05, 25.59) * mm});
            skPoint(sketch, "E327.visualSharp", {"position": v(-143.04, 15.88) * mm});
            skArc(sketch, "E327.filletArc", {"start": v(-147.44, 18.25) * mm, "mid": v(-145.3, 17.98) * mm, "end": v(-143.54, 19.2) * mm});
            skPoint(sketch, "E328.visualSharp", {"position": v(-159.68, 34.47) * mm});
            skArc(sketch, "E328.filletArc", {"start": v(-158.52, 34.84) * mm, "mid": v(-159.52, 34.29) * mm, "end": v(-160.25, 33.4) * mm});
            skPoint(sketch, "E329.visualSharp", {"position": v(-156.28, 40.73) * mm});
            skArc(sketch, "E329.filletArc", {"start": v(-153.84, 46.72) * mm, "mid": v(-153.26, 43.54) * mm, "end": v(-150.13, 42.73) * mm});
            skPoint(sketch, "E330.visualSharp", {"position": v(-135.15, 67.18) * mm});
            skArc(sketch, "E330.filletArc", {"start": v(-134.1, 64.64) * mm, "mid": v(-135.6, 66.21) * mm, "end": v(-137.78, 66.35) * mm});
            skPoint(sketch, "E331.visualSharp", {"position": v(-147.03, 63.43) * mm});
            skArc(sketch, "E331.filletArc", {"start": v(-145.68, 63.86) * mm, "mid": v(-146.81, 63.2) * mm, "end": v(-147.56, 62.13) * mm});
            skPoint(sketch, "E332.visualSharp", {"position": v(-128.04, 49.93) * mm});
            skArc(sketch, "E332.filletArc", {"start": v(-131.12, 48.93) * mm, "mid": v(-129.32, 50.53) * mm, "end": v(-129.27, 52.93) * mm});
            skPoint(sketch, "E333.visualSharp", {"position": v(-128.61, 44.28) * mm});
            skArc(sketch, "E333.filletArc", {"start": v(-127.56, 41.74) * mm, "mid": v(-129.07, 43.31) * mm, "end": v(-131.24, 43.45) * mm});
            skPoint(sketch, "E334.visualSharp", {"position": v(-124.21, 33.6) * mm});
            skArc(sketch, "E334.filletArc", {"start": v(-125.36, 32.22) * mm, "mid": v(-124.7, 33.68) * mm, "end": v(-124.9, 35.27) * mm});
            skPoint(sketch, "E335.visualSharp", {"position": v(-136.09, 10.78) * mm});
            skArc(sketch, "E335.filletArc", {"start": v(-134.4, 13) * mm, "mid": v(-135, 10.89) * mm, "end": v(-134.01, 8.94) * mm});
            skPoint(sketch, "E336.visualSharp", {"position": v(-123.41, 27.42) * mm});
            skArc(sketch, "E336.filletArc", {"start": v(-121.94, 27.43) * mm, "mid": v(-123.26, 27.11) * mm, "end": v(-124.3, 26.24) * mm});
            skPoint(sketch, "E337.visualSharp", {"position": v(-120.37, -3.23) * mm});
            skArc(sketch, "E337.filletArc", {"start": v(-123.2, -0.7) * mm, "mid": v(-120.69, -1.42) * mm, "end": v(-118.57, 0.11) * mm});
            skPoint(sketch, "E338.visualSharp", {"position": v(-109.19, 27.48) * mm});
            skArc(sketch, "E338.filletArc", {"start": v(-111.3, 23.15) * mm, "mid": v(-111.46, 26.06) * mm, "end": v(-114.01, 27.46) * mm});
            skPoint(sketch, "E339.visualSharp", {"position": v(-160.85, -78.35) * mm});
            skPoint(sketch, "E340.visualSharp", {"position": v(-117.84, 32.98) * mm});
            skArc(sketch, "E340.filletArc", {"start": v(-118.5, 35.9) * mm, "mid": v(-117.18, 34.03) * mm, "end": v(-114.91, 33.65) * mm});
            skPoint(sketch, "E341.visualSharp", {"position": v(-94.3, 48.17) * mm});
            skArc(sketch, "E341.filletArc", {"start": v(-98.5, 43.54) * mm, "mid": v(-97.94, 46.69) * mm, "end": v(-100.53, 48.55) * mm});
            skPoint(sketch, "E342.visualSharp", {"position": v(-121.71, 49.86) * mm});
            skArc(sketch, "E342.filletArc", {"start": v(-117.7, 49.61) * mm, "mid": v(-120.18, 48.56) * mm, "end": v(-120.82, 45.95) * mm});
            skPoint(sketch, "E343.visualSharp", {"position": v(-105.51, 35.81) * mm});
            skArc(sketch, "E343.filletArc", {"start": v(-106.43, 35.6) * mm, "mid": v(-105.58, 35.94) * mm, "end": v(-104.88, 36.5) * mm});
            skPoint(sketch, "E344.visualSharp", {"position": v(-122.29, 52.35) * mm});
            skArc(sketch, "E344.filletArc", {"start": v(-122.78, 54.48) * mm, "mid": v(-121.82, 52.89) * mm, "end": v(-120.1, 52.17) * mm});
            skPoint(sketch, "E345.visualSharp", {"position": v(-123.76, 58.77) * mm});
            skArc(sketch, "E345.filletArc", {"start": v(-122.01, 59.91) * mm, "mid": v(-123.15, 58.52) * mm, "end": v(-123.3, 56.73) * mm});
            skPoint(sketch, "E346.visualSharp", {"position": v(-105.85, 70.5) * mm});
            skArc(sketch, "E346.filletArc", {"start": v(-104.22, 67.94) * mm, "mid": v(-106.12, 69.27) * mm, "end": v(-108.4, 68.84) * mm});
            skPoint(sketch, "E347.visualSharp", {"position": v(-109.23, 74.82) * mm});
            skArc(sketch, "E347.filletArc", {"start": v(-114.66, 72.1) * mm, "mid": v(-113, 74.8) * mm, "end": v(-114.69, 77.49) * mm});
            skPoint(sketch, "E348.visualSharp", {"position": v(-122.14, 81.13) * mm});
            skArc(sketch, "E348.filletArc", {"start": v(-118.88, 79.53) * mm, "mid": v(-121.43, 79.57) * mm, "end": v(-123.09, 77.62) * mm});
            skPoint(sketch, "E349.visualSharp", {"position": v(-92.73, 49.9) * mm});
            skArc(sketch, "E349.filletArc", {"start": v(-98.75, 50.4) * mm, "mid": v(-95.94, 51.83) * mm, "end": v(-95.97, 55) * mm});
            skPoint(sketch, "E350.visualSharp", {"position": v(-126.14, 66.37) * mm});
            skArc(sketch, "E350.filletArc", {"start": v(-124.39, 72.83) * mm, "mid": v(-123.39, 69.73) * mm, "end": v(-120.15, 69.36) * mm});
            skPoint(sketch, "E351.visualSharp", {"position": v(-130.47, 75.44) * mm});
            skArc(sketch, "E351.filletArc", {"start": v(-132.24, 75.15) * mm, "mid": v(-130.79, 75.82) * mm, "end": v(-129.88, 77.13) * mm});
            skPoint(sketch, "E352.visualSharp", {"position": v(-146, 72.96) * mm});
            skArc(sketch, "E352.filletArc", {"start": v(-144, 77.9) * mm, "mid": v(-143.57, 74.9) * mm, "end": v(-140.74, 73.8) * mm});
            skPoint(sketch, "E353.visualSharp", {"position": v(-119.53, 106.94) * mm});
            skArc(sketch, "E353.filletArc", {"start": v(-120.1, 105.31) * mm, "mid": v(-119.99, 106.85) * mm, "end": v(-120.66, 108.25) * mm});
            skPoint(sketch, "E354.visualSharp", {"position": v(-128.1, 116.9) * mm});
            skArc(sketch, "E354.filletArc", {"start": v(-124.9, 113.18) * mm, "mid": v(-127.66, 114.18) * mm, "end": v(-129.95, 112.35) * mm});
            skPoint(sketch, "E355.visualSharp", {"position": v(-93.08, 122.23) * mm});
            skArc(sketch, "E355.filletArc", {"start": v(-97.28, 122.33) * mm, "mid": v(-94.8, 123.53) * mm, "end": v(-94.35, 126.23) * mm});
            skPoint(sketch, "E356.visualSharp", {"position": v(-96.66, 133.55) * mm});
            skArc(sketch, "E356.filletArc", {"start": v(-95.76, 130.7) * mm, "mid": v(-97.23, 132.45) * mm, "end": v(-99.52, 132.65) * mm});
            skPoint(sketch, "E357.visualSharp", {"position": v(-126.2, 123.03) * mm});
            skArc(sketch, "E357.filletArc", {"start": v(-124.57, 127.06) * mm, "mid": v(-124.3, 124.28) * mm, "end": v(-121.86, 122.93) * mm});
            skPoint(sketch, "E358.visualSharp", {"position": v(-109.76, 129.41) * mm});
            skArc(sketch, "E358.filletArc", {"start": v(-110.76, 129.82) * mm, "mid": v(-109.75, 129.6) * mm, "end": v(-108.72, 129.74) * mm});
            skPoint(sketch, "E359.visualSharp", {"position": v(-121.63, 134.26) * mm});
            skArc(sketch, "E359.filletArc", {"start": v(-118.85, 133.12) * mm, "mid": v(-121.15, 133.1) * mm, "end": v(-122.76, 131.48) * mm});
            skPoint(sketch, "E360.visualSharp", {"position": v(-121.81, 118.75) * mm});
            skArc(sketch, "E360.filletArc", {"start": v(-115.45, 118.58) * mm, "mid": v(-118.21, 116.93) * mm, "end": v(-117.9, 113.73) * mm});
            skPoint(sketch, "E361.visualSharp", {"position": v(-114.7, 84.61) * mm});
            skArc(sketch, "E361.filletArc", {"start": v(-113.88, 91.76) * mm, "mid": v(-112.36, 88.8) * mm, "end": v(-109.05, 89.07) * mm});
            skPoint(sketch, "E362.visualSharp", {"position": v(-88.74, 105.07) * mm});
            skArc(sketch, "E362.filletArc", {"start": v(-89.93, 104.13) * mm, "mid": v(-89.06, 105.22) * mm, "end": v(-88.78, 106.58) * mm});
            skPoint(sketch, "E363.visualSharp", {"position": v(-112.21, 106.43) * mm});
            skArc(sketch, "E363.filletArc", {"start": v(-112.35, 105.21) * mm, "mid": v(-112.45, 106.36) * mm, "end": v(-112.97, 107.4) * mm});
            skPoint(sketch, "E364.visualSharp", {"position": v(-85.63, 120.13) * mm});
            skArc(sketch, "E364.filletArc", {"start": v(-86.56, 123.52) * mm, "mid": v(-84.94, 121.6) * mm, "end": v(-82.43, 121.58) * mm});
            skPoint(sketch, "E365.visualSharp", {"position": v(-87.95, 154.92) * mm});
            skArc(sketch, "E365.filletArc", {"start": v(-83.68, 152.57) * mm, "mid": v(-86.61, 152.56) * mm, "end": v(-88.13, 150.06) * mm});
            skPoint(sketch, "E366.visualSharp", {"position": v(-71.16, 126.7) * mm});
            skArc(sketch, "E366.filletArc", {"start": v(-72.98, 125.87) * mm, "mid": v(-71.68, 127.02) * mm, "end": v(-71.23, 128.7) * mm});
            skPoint(sketch, "E367.visualSharp", {"position": v(-93.17, 145.83) * mm});
            skArc(sketch, "E367.filletArc", {"start": v(-94.5, 144.98) * mm, "mid": v(-93.5, 146.02) * mm, "end": v(-93.11, 147.4) * mm});
            skPoint(sketch, "E368.visualSharp", {"position": v(-108.31, 136.18) * mm});
            skArc(sketch, "E368.filletArc", {"start": v(-109.75, 136.77) * mm, "mid": v(-108.35, 136.56) * mm, "end": v(-107, 137.02) * mm});
            skPoint(sketch, "E369.visualSharp", {"position": v(-121.2, 141.43) * mm});
            skArc(sketch, "E369.filletArc", {"start": v(-120.37, 144.07) * mm, "mid": v(-120.22, 141.9) * mm, "end": v(-118.64, 140.4) * mm});
            skPoint(sketch, "E370.visualSharp", {"position": v(-112.58, 168.96) * mm});
            skArc(sketch, "E370.filletArc", {"start": v(-109.44, 167.42) * mm, "mid": v(-111.95, 167.48) * mm, "end": v(-113.62, 165.62) * mm});
            skPoint(sketch, "E371.visualSharp", {"position": v(-92.7, 159.25) * mm});
            skArc(sketch, "E371.filletArc", {"start": v(-92.77, 157.3) * mm, "mid": v(-93.2, 158.96) * mm, "end": v(-94.45, 160.1) * mm});
            skPoint(sketch, "E372.visualSharp", {"position": v(-60.08, 134.93) * mm});
            skArc(sketch, "E372.filletArc", {"start": v(-55.44, 133.64) * mm, "mid": v(-58.27, 132.96) * mm, "end": v(-59.2, 130.2) * mm});
            skPoint(sketch, "E373.visualSharp", {"position": v(-40.42, 110.45) * mm});
            skArc(sketch, "E373.filletArc", {"start": v(-41.06, 110.03) * mm, "mid": v(-40.5, 110.51) * mm, "end": v(-40.06, 111.12) * mm});
            skPoint(sketch, "E374.visualSharp", {"position": v(-47.53, 105.79) * mm});
            skArc(sketch, "E374.filletArc", {"start": v(-49.04, 108.8) * mm, "mid": v(-47.14, 107.24) * mm, "end": v(-44.72, 107.63) * mm});
            skPoint(sketch, "E375.visualSharp", {"position": v(-39.26, 128.05) * mm});
            skArc(sketch, "E375.filletArc", {"start": v(-39.83, 128.28) * mm, "mid": v(-39.25, 128.1) * mm, "end": v(-38.65, 128.06) * mm});
            skArc(sketch, "E376.filletArc", {"start": v(-33.3, 123.68) * mm, "mid": v(-33.37, 126.66) * mm, "end": v(-35.98, 128.1) * mm});
            skPoint(sketch, "E377.visualSharp", {"position": v(-28.16, 114.87) * mm});
            skPoint(sketch, "E378.visualSharp", {"position": v(-28.7, 112.79) * mm});
            skPoint(sketch, "E379.visualSharp", {"position": v(-41.47, 75.3) * mm});
            skPoint(sketch, "E380.visualSharp", {"position": v(-28.65, 72.85) * mm});
            skPoint(sketch, "E381.visualSharp", {"position": v(-47.6, 76.46) * mm});
            skArc(sketch, "E381.filletArc", {"start": v(-49.32, 76.79) * mm, "mid": v(-47.76, 76.9) * mm, "end": v(-46.47, 77.8) * mm});
            skPoint(sketch, "E382.visualSharp", {"position": v(-54.3, 77.73) * mm});
            skArc(sketch, "E382.filletArc", {"start": v(-54.76, 79.6) * mm, "mid": v(-53.9, 78.14) * mm, "end": v(-52.4, 77.38) * mm});
            skPoint(sketch, "E383.visualSharp", {"position": v(-58.13, 93.28) * mm});
            skArc(sketch, "E383.filletArc", {"start": v(-55.82, 94.3) * mm, "mid": v(-57.3, 92.87) * mm, "end": v(-57.53, 90.83) * mm});
            skPoint(sketch, "E384.visualSharp", {"position": v(-32.34, 94.62) * mm});
            skArc(sketch, "E384.filletArc", {"start": v(-34.27, 92.32) * mm, "mid": v(-33.58, 94.51) * mm, "end": v(-34.64, 96.55) * mm});
            skPoint(sketch, "E385.visualSharp", {"position": v(-40.14, 101.17) * mm});
            skArc(sketch, "E385.filletArc", {"start": v(-38.71, 99.97) * mm, "mid": v(-40.22, 100.64) * mm, "end": v(-41.85, 100.42) * mm});
            skPoint(sketch, "E386.visualSharp", {"position": v(-69.33, 93.43) * mm});
            skArc(sketch, "E386.filletArc", {"start": v(-70.96, 94.51) * mm, "mid": v(-69.33, 94.01) * mm, "end": v(-67.69, 94.48) * mm});
            skPoint(sketch, "E387.visualSharp", {"position": v(-84.15, 103.28) * mm});
            skArc(sketch, "E387.filletArc", {"start": v(-83.23, 105.56) * mm, "mid": v(-83.32, 103.54) * mm, "end": v(-82.11, 101.93) * mm});
            skPoint(sketch, "E388.visualSharp", {"position": v(-79.93, 113.64) * mm});
            skArc(sketch, "E388.filletArc", {"start": v(-79.13, 114.16) * mm, "mid": v(-79.82, 113.55) * mm, "end": v(-80.3, 112.76) * mm});
            skPoint(sketch, "E389.visualSharp", {"position": v(-63.36, 124.2) * mm});
            skArc(sketch, "E389.filletArc", {"start": v(-61.95, 120.99) * mm, "mid": v(-63.83, 122.65) * mm, "end": v(-66.31, 122.31) * mm});
            skPoint(sketch, "E390.visualSharp", {"position": v(-54.12, 103.12) * mm});
            skArc(sketch, "E390.filletArc", {"start": v(-56.29, 101.74) * mm, "mid": v(-55.03, 103.4) * mm, "end": v(-55.15, 105.48) * mm});
            skPoint(sketch, "E391.visualSharp", {"position": v(-65.43, 87.84) * mm});
            skArc(sketch, "E391.filletArc", {"start": v(-64.35, 84.42) * mm, "mid": v(-66.07, 86.3) * mm, "end": v(-68.6, 86.18) * mm});
            skPoint(sketch, "E392.visualSharp", {"position": v(-88.7, 54.91) * mm});
            skArc(sketch, "E392.filletArc", {"start": v(-90.55, 58.62) * mm, "mid": v(-88.35, 57) * mm, "end": v(-85.75, 57.83) * mm});
            skPoint(sketch, "E393.visualSharp", {"position": v(-97.76, 73.04) * mm});
            skArc(sketch, "E393.filletArc", {"start": v(-94.66, 74.21) * mm, "mid": v(-96.39, 72.5) * mm, "end": v(-96.28, 70.06) * mm});
            skPoint(sketch, "E394.visualSharp", {"position": v(-61.16, 74.33) * mm});
            skArc(sketch, "E394.filletArc", {"start": v(-63.7, 73.28) * mm, "mid": v(-62.13, 74.78) * mm, "end": v(-61.99, 76.95) * mm});
            skPoint(sketch, "E395.visualSharp", {"position": v(-74.64, 90.8) * mm});
            skArc(sketch, "E395.filletArc", {"start": v(-78.9, 88.39) * mm, "mid": v(-77.37, 90.9) * mm, "end": v(-78.71, 93.5) * mm});
            skPoint(sketch, "E396.visualSharp", {"position": v(-87.35, 99.24) * mm});
            skArc(sketch, "E396.filletArc", {"start": v(-85.63, 98.1) * mm, "mid": v(-87.34, 98.6) * mm, "end": v(-89.04, 98.04) * mm});
            skPoint(sketch, "E397.visualSharp", {"position": v(-110.34, 82.83) * mm});
            skArc(sketch, "E397.filletArc", {"start": v(-107.03, 85.2) * mm, "mid": v(-108.28, 82.8) * mm, "end": v(-107.1, 80.37) * mm});
            skPoint(sketch, "E398.visualSharp", {"position": v(-101.12, 75.82) * mm});
            skArc(sketch, "E398.filletArc", {"start": v(-102.7, 77.02) * mm, "mid": v(-101.08, 76.41) * mm, "end": v(-99.4, 76.8) * mm});
            skPoint(sketch, "E399.visualSharp", {"position": v(-89.14, 117.85) * mm});
            skArc(sketch, "E399.filletArc", {"start": v(-89.05, 115.02) * mm, "mid": v(-89.93, 117.05) * mm, "end": v(-91.96, 117.93) * mm});
            skPoint(sketch, "E400.visualSharp", {"position": v(-36.57, 104.52) * mm});
            skPoint(sketch, "E401.visualSharp", {"position": v(-71.6, 140.51) * mm});
            skArc(sketch, "E401.filletArc", {"start": v(-71.56, 139.56) * mm, "mid": v(-71.73, 140.46) * mm, "end": v(-72.17, 141.28) * mm});
            skPoint(sketch, "E402.visualSharp", {"position": v(-137.5, 6.94) * mm});
            skArc(sketch, "E402.filletArc", {"start": v(-135.15, 4.84) * mm, "mid": v(-137.4, 5.6) * mm, "end": v(-139.48, 4.49) * mm});
            skPoint(sketch, "E403.visualSharp", {"position": v(-121.91, -7) * mm});
            skArc(sketch, "E403.filletArc", {"start": v(-122.7, -8.97) * mm, "mid": v(-122.56, -7.16) * mm, "end": v(-123.49, -5.6) * mm});
            skPoint(sketch, "E404.visualSharp", {"position": v(-145.1, -2.46) * mm});
            skArc(sketch, "E404.filletArc", {"start": v(-143.56, -0.56) * mm, "mid": v(-144.23, -2.46) * mm, "end": v(-143.55, -4.35) * mm});
            skPoint(sketch, "E405.visualSharp", {"position": v(-140.1, 14.3) * mm});
            skArc(sketch, "E405.filletArc", {"start": v(-140.46, 22.1) * mm, "mid": v(-138.41, 19.4) * mm, "end": v(-135.14, 20.33) * mm});
            skLineSegment(sketch, "E406", {"start": v(-143.54, 19.2) * mm, "end": v(-144.02, 35.41) * mm});
            skArc(sketch, "E407.filletArc", {"start": v(-144.02, 35.41) * mm, "mid": v(-145.29, 37.77) * mm, "end": v(-147.93, 38.18) * mm});
            skLineSegment(sketch, "E408.0", {"start": v(-110.34, 82.83) * mm, "end": v(-114.7, 84.61) * mm, "construction": true});
            skLineSegment(sketch, "E409.0", {"start": v(-128.36, -22.82) * mm, "end": v(-169.22, -6.17) * mm, "construction": true});
            skLineSegment(sketch, "E410.0", {"start": v(-109.19, 27.48) * mm, "end": v(-124.21, 33.6) * mm, "construction": true});
            skLineSegment(sketch, "E411.0", {"start": v(-92.73, 49.9) * mm, "end": v(-135.15, 67.18) * mm, "construction": true});
            skLineSegment(sketch, "E412.0", {"start": v(-13.28, 86.48) * mm, "end": v(-79.93, 113.64) * mm, "construction": true});
            skLineSegment(sketch, "E413.0", {"start": v(-28.65, 72.85) * mm, "end": v(-65.43, 87.84) * mm, "construction": true});
            skLineSegment(sketch, "E414.0", {"start": v(-0.86, 119.43) * mm, "end": v(-87.95, 154.92) * mm, "construction": true});
            skLineSegment(sketch, "E415.0", {"start": v(-128.04, 49.93) * mm, "end": v(-149.24, -2.08) * mm, "construction": true});
            skLineSegment(sketch, "E416.0", {"start": v(-120.37, -3.23) * mm, "end": v(-128.36, -22.82) * mm, "construction": true});
            skLineSegment(sketch, "E417.0", {"start": v(-54.12, 103.12) * mm, "end": v(-58.13, 93.28) * mm, "construction": true});
            skLineSegment(sketch, "E418.0", {"start": v(-58.82, 128.2) * mm, "end": v(-88.7, 54.91) * mm, "construction": true});
            skLineSegment(sketch, "E419.0", {"start": v(-39.26, 128.05) * mm, "end": v(-61.16, 74.33) * mm, "construction": true});
            skLineSegment(sketch, "E420", {"start": v(-72.07, 148.45) * mm, "end": v(-64.04, 137.72) * mm});
            skLineSegment(sketch, "E421", {"start": v(-64.04, 137.72) * mm, "end": v(-55.15, 137.72) * mm});
            skLineSegment(sketch, "E422", {"start": v(-55.15, 137.72) * mm, "end": v(-51.02, 136.04) * mm});
            skLineSegment(sketch, "E423", {"start": v(-46.97, 139.53) * mm, "end": v(-50.3, 153.16) * mm});
            skLineSegment(sketch, "E424", {"start": v(-52.86, 155.43) * mm, "end": v(-81.82, 158.84) * mm});
            skLineSegment(sketch, "E425", {"start": v(-81.82, 158.84) * mm, "end": v(-72.07, 148.45) * mm});
            skLineSegment(sketch, "E426", {"start": v(-41.86, 154.98) * mm, "end": v(-34.6, 154.98) * mm});
            skLineSegment(sketch, "E427", {"start": v(-34.6, 154.98) * mm, "end": v(-33.69, 135.75) * mm});
            skLineSegment(sketch, "E428", {"start": v(-36.54, 132.6) * mm, "end": v(-38.42, 132.52) * mm});
            skLineSegment(sketch, "E429", {"start": v(-41.5, 134.93) * mm, "end": v(-44.8, 151.39) * mm});
            skLineSegment(sketch, "E430", {"start": v(-111.3, 23.15) * mm, "end": v(-118.57, 0.11) * mm});
            skLineSegment(sketch, "E431", {"start": v(-57.16, 73.43) * mm, "end": v(-48.09, 71.08) * mm});
            skLineSegment(sketch, "E432", {"start": v(-46.3, 66.58) * mm, "end": v(-55.09, 52.58) * mm});
            skLineSegment(sketch, "E433", {"start": v(-55.86, 51.75) * mm, "end": v(-59.96, 48.77) * mm});
            skLineSegment(sketch, "E434", {"start": v(-64.45, 49.93) * mm, "end": v(-70.9, 63.87) * mm});
            skLineSegment(sketch, "E435", {"start": v(-69.57, 67.78) * mm, "end": v(-59.3, 73.19) * mm});
            skLineSegment(sketch, "E436", {"start": v(-73.12, 58.57) * mm, "end": v(-68.01, 46.95) * mm});
            skLineSegment(sketch, "E437", {"start": v(-69.55, 43) * mm, "end": v(-77.71, 39.4) * mm});
            skLineSegment(sketch, "E438", {"start": v(-81.66, 40.95) * mm, "end": v(-85.49, 49.64) * mm});
            skLineSegment(sketch, "E439", {"start": v(-84.8, 53.03) * mm, "end": v(-77.93, 59.54) * mm});
            skLineSegment(sketch, "E440", {"start": v(-99.08, 33.3) * mm, "end": v(-96.73, 31.45) * mm});
            skLineSegment(sketch, "E441", {"start": v(-92.76, 31.67) * mm, "end": v(-89.41, 35) * mm});
            skLineSegment(sketch, "E442", {"start": v(-88.5, 35.62) * mm, "end": v(-86.56, 36.47) * mm});
            skLineSegment(sketch, "E443", {"start": v(-85.28, 40.89) * mm, "end": v(-88.53, 45.74) * mm});
            skLineSegment(sketch, "E444", {"start": v(-93.44, 45.85) * mm, "end": v(-99.63, 37.43) * mm});
            skLineSegment(sketch, "E445", {"start": v(-108, 28.17) * mm, "end": v(-107.52, 27.06) * mm});
            skLineSegment(sketch, "E446", {"start": v(-107.3, 25.36) * mm, "end": v(-109.16, 14.36) * mm});
            skLineSegment(sketch, "E447", {"start": v(-109.23, 14.05) * mm, "end": v(-110.37, 9.96) * mm});
            skLineSegment(sketch, "E448", {"start": v(-107.85, 6.17) * mm, "end": v(-104.33, 5.73) * mm});
            skLineSegment(sketch, "E449", {"start": v(-100.98, 8.33) * mm, "end": v(-100, 16.13) * mm});
            skLineSegment(sketch, "E450", {"start": v(-99.89, 16.66) * mm, "end": v(-98.17, 22.1) * mm});
            skLineSegment(sketch, "E451", {"start": v(-99.6, 25.64) * mm, "end": v(-106.62, 29.46) * mm});
            skLineSegment(sketch, "E452", {"start": v(-115.16, -10.32) * mm, "end": v(-102.95, -14.17) * mm});
            skLineSegment(sketch, "E453", {"start": v(-100.94, -16.3) * mm, "end": v(-99.59, -21.67) * mm});
            skLineSegment(sketch, "E454", {"start": v(-102.91, -25.38) * mm, "end": v(-117.43, -23.33) * mm});
            skLineSegment(sketch, "E455", {"start": v(-119.98, -19.97) * mm, "end": v(-119.04, -12.78) * mm});
            skLineSegment(sketch, "E456", {"start": v(-113.95, 1.3) * mm, "end": v(-115.58, -2.7) * mm});
            skLineSegment(sketch, "E457", {"start": v(-113.7, -6.7) * mm, "end": v(-106.1, -9.09) * mm});
            skLineSegment(sketch, "E458", {"start": v(-102.2, -6.2) * mm, "end": v(-102.25, -0.62) * mm});
            skLineSegment(sketch, "E459", {"start": v(-104.84, 2.33) * mm, "end": v(-110.76, 3.15) * mm});
            skPoint(sketch, "E460.visualSharp", {"position": v(-113.07, 3.46) * mm});
            skArc(sketch, "E460.filletArc", {"start": v(-110.76, 3.15) * mm, "mid": v(-112.67, 2.77) * mm, "end": v(-113.95, 1.3) * mm});
            skPoint(sketch, "E461.visualSharp", {"position": v(-102.18, -10.33) * mm});
            skArc(sketch, "E461.filletArc", {"start": v(-106.1, -9.09) * mm, "mid": v(-103.42, -8.64) * mm, "end": v(-102.2, -6.2) * mm});
            skPoint(sketch, "E462.visualSharp", {"position": v(-116.81, -5.71) * mm});
            skArc(sketch, "E462.filletArc", {"start": v(-115.58, -2.7) * mm, "mid": v(-115.52, -5.1) * mm, "end": v(-113.7, -6.7) * mm});
            skPoint(sketch, "E463.visualSharp", {"position": v(-98.5, -26) * mm});
            skArc(sketch, "E463.filletArc", {"start": v(-102.91, -25.38) * mm, "mid": v(-100.26, -24.41) * mm, "end": v(-99.59, -21.67) * mm});
            skPoint(sketch, "E464.visualSharp", {"position": v(-102.26, 1.98) * mm});
            skArc(sketch, "E464.filletArc", {"start": v(-102.25, -0.62) * mm, "mid": v(-103, 1.34) * mm, "end": v(-104.84, 2.33) * mm});
            skPoint(sketch, "E465.visualSharp", {"position": v(-118.57, -9.24) * mm});
            skArc(sketch, "E465.filletArc", {"start": v(-115.16, -10.32) * mm, "mid": v(-117.67, -10.65) * mm, "end": v(-119.04, -12.78) * mm});
            skPoint(sketch, "E466.visualSharp", {"position": v(-120.37, -22.91) * mm});
            skArc(sketch, "E466.filletArc", {"start": v(-119.98, -19.97) * mm, "mid": v(-119.4, -22.17) * mm, "end": v(-117.43, -23.33) * mm});
            skPoint(sketch, "E467.visualSharp", {"position": v(-101.35, -14.67) * mm});
            skArc(sketch, "E467.filletArc", {"start": v(-100.94, -16.3) * mm, "mid": v(-101.67, -14.97) * mm, "end": v(-102.95, -14.17) * mm});
            skPoint(sketch, "E468.visualSharp", {"position": v(-111.3, 6.6) * mm});
            skArc(sketch, "E468.filletArc", {"start": v(-110.37, 9.96) * mm, "mid": v(-109.98, 7.49) * mm, "end": v(-107.85, 6.17) * mm});
            skPoint(sketch, "E469.visualSharp", {"position": v(-97.43, 24.46) * mm});
            skArc(sketch, "E469.filletArc", {"start": v(-98.17, 22.1) * mm, "mid": v(-98.25, 24.13) * mm, "end": v(-99.6, 25.64) * mm});
            skPoint(sketch, "E470.visualSharp", {"position": v(-99.97, 16.4) * mm});
            skArc(sketch, "E470.filletArc", {"start": v(-99.89, 16.66) * mm, "mid": v(-99.96, 16.4) * mm, "end": v(-100, 16.13) * mm});
            skPoint(sketch, "E471.visualSharp", {"position": v(-101.35, 5.36) * mm});
            skArc(sketch, "E471.filletArc", {"start": v(-104.33, 5.73) * mm, "mid": v(-102.11, 6.34) * mm, "end": v(-100.98, 8.33) * mm});
            skPoint(sketch, "E472.visualSharp", {"position": v(-107.16, 26.24) * mm});
            skArc(sketch, "E472.filletArc", {"start": v(-107.3, 25.36) * mm, "mid": v(-107.29, 26.22) * mm, "end": v(-107.52, 27.06) * mm});
            skPoint(sketch, "E473.visualSharp", {"position": v(-109.19, 14.2) * mm});
            skArc(sketch, "E473.filletArc", {"start": v(-109.23, 14.05) * mm, "mid": v(-109.2, 14.2) * mm, "end": v(-109.16, 14.36) * mm});
            skPoint(sketch, "E474.visualSharp", {"position": v(-109.19, 30.85) * mm});
            skArc(sketch, "E474.filletArc", {"start": v(-106.62, 29.46) * mm, "mid": v(-107.77, 29.31) * mm, "end": v(-108, 28.17) * mm});
            skPoint(sketch, "E475.visualSharp", {"position": v(-90.9, 49.29) * mm});
            skArc(sketch, "E475.filletArc", {"start": v(-88.53, 45.74) * mm, "mid": v(-90.95, 47.07) * mm, "end": v(-93.44, 45.85) * mm});
            skPoint(sketch, "E476.visualSharp", {"position": v(-83.28, 37.91) * mm});
            skArc(sketch, "E476.filletArc", {"start": v(-86.56, 36.47) * mm, "mid": v(-84.89, 38.38) * mm, "end": v(-85.28, 40.89) * mm});
            skPoint(sketch, "E477.visualSharp", {"position": v(-89.02, 35.4) * mm});
            skArc(sketch, "E477.filletArc", {"start": v(-88.5, 35.62) * mm, "mid": v(-88.99, 35.35) * mm, "end": v(-89.41, 35) * mm});
            skPoint(sketch, "E478.visualSharp", {"position": v(-94.65, 29.8) * mm});
            skArc(sketch, "E478.filletArc", {"start": v(-96.73, 31.45) * mm, "mid": v(-94.7, 30.8) * mm, "end": v(-92.76, 31.67) * mm});
            skPoint(sketch, "E479.visualSharp", {"position": v(-101.35, 35.1) * mm});
            skArc(sketch, "E479.filletArc", {"start": v(-99.63, 37.43) * mm, "mid": v(-100.2, 35.25) * mm, "end": v(-99.08, 33.3) * mm});
            skPoint(sketch, "E480.visualSharp", {"position": v(-66.8, 44.2) * mm});
            skArc(sketch, "E480.filletArc", {"start": v(-69.55, 43) * mm, "mid": v(-67.96, 44.65) * mm, "end": v(-68.01, 46.95) * mm});
            skPoint(sketch, "E481.visualSharp", {"position": v(-86.34, 51.58) * mm});
            skArc(sketch, "E481.filletArc", {"start": v(-84.8, 53.03) * mm, "mid": v(-85.68, 51.44) * mm, "end": v(-85.49, 49.64) * mm});
            skPoint(sketch, "E482.visualSharp", {"position": v(-80.46, 38.2) * mm});
            skArc(sketch, "E482.filletArc", {"start": v(-81.66, 40.95) * mm, "mid": v(-80, 39.36) * mm, "end": v(-77.71, 39.4) * mm});
            skPoint(sketch, "E483.visualSharp", {"position": v(-74.84, 62.47) * mm});
            skArc(sketch, "E483.filletArc", {"start": v(-73.12, 58.57) * mm, "mid": v(-75.27, 60.3) * mm, "end": v(-77.93, 59.54) * mm});
            skPoint(sketch, "E484.visualSharp", {"position": v(-72.1, 66.46) * mm});
            skArc(sketch, "E484.filletArc", {"start": v(-69.57, 67.78) * mm, "mid": v(-71.01, 66.1) * mm, "end": v(-70.9, 63.87) * mm});
            skPoint(sketch, "E485.visualSharp", {"position": v(-58.28, 73.73) * mm});
            skArc(sketch, "E485.filletArc", {"start": v(-57.16, 73.43) * mm, "mid": v(-58.26, 73.51) * mm, "end": v(-59.3, 73.19) * mm});
            skPoint(sketch, "E486.visualSharp", {"position": v(-44.12, 70.05) * mm});
            skArc(sketch, "E486.filletArc", {"start": v(-46.3, 66.58) * mm, "mid": v(-46.05, 69.29) * mm, "end": v(-48.09, 71.08) * mm});
            skPoint(sketch, "E487.visualSharp", {"position": v(-55.4, 52.09) * mm});
            skArc(sketch, "E487.filletArc", {"start": v(-55.86, 51.75) * mm, "mid": v(-55.44, 52.13) * mm, "end": v(-55.09, 52.58) * mm});
            skPoint(sketch, "E488.visualSharp", {"position": v(-62.91, 46.61) * mm});
            skArc(sketch, "E488.filletArc", {"start": v(-64.45, 49.93) * mm, "mid": v(-62.48, 48.29) * mm, "end": v(-59.96, 48.77) * mm});
            skPoint(sketch, "E489.visualSharp", {"position": v(-45.52, 154.98) * mm});
            skArc(sketch, "E489.filletArc", {"start": v(-41.86, 154.98) * mm, "mid": v(-44.18, 153.88) * mm, "end": v(-44.8, 151.39) * mm});
            skPoint(sketch, "E490.visualSharp", {"position": v(-41, 132.4) * mm});
            skArc(sketch, "E490.filletArc", {"start": v(-41.5, 134.93) * mm, "mid": v(-40.4, 133.15) * mm, "end": v(-38.42, 132.52) * mm});
            skPoint(sketch, "E491.visualSharp", {"position": v(-33.55, 132.75) * mm});
            skArc(sketch, "E491.filletArc", {"start": v(-36.54, 132.6) * mm, "mid": v(-34.47, 133.59) * mm, "end": v(-33.69, 135.75) * mm});
            skPoint(sketch, "E492.visualSharp", {"position": v(-50.79, 155.19) * mm});
            skArc(sketch, "E492.filletArc", {"start": v(-50.3, 153.16) * mm, "mid": v(-51.22, 154.7) * mm, "end": v(-52.86, 155.43) * mm});
            skPoint(sketch, "E493.visualSharp", {"position": v(-45.58, 133.82) * mm});
            skArc(sketch, "E493.filletArc", {"start": v(-51.02, 136.04) * mm, "mid": v(-47.93, 136.55) * mm, "end": v(-46.97, 139.53) * mm});
            skSolve(sketch);
        }
        {
            var Q0;
            Q0 = qSketchRegion(id + "F1", true);
            var Q1;
            Q1 = qSketchRegion(id + "F0", true);
            extrude(context, id + "F4", {"entities" : qUnion([Q0, Q1]), "depth" : 3 * mm});
        }
        {
            var Q0;
            Q0 = qSketchRegion(id + "F2", true);
            extrude(context, id + "F5", {"entities" : qUnion([Q0]), "endBound" : BoundingType.SYMMETRIC, "oppositeDirection" : true, "depth" : 25 * mm});
        }
        {
            var Q0;
            Q0 = qSketchRegion(id + "F3", true);
            extrude(context, id + "F6", {"entities" : qUnion([Q0]), "operationType" : NewBodyOperationType.REMOVE, "endBound" : BoundingType.SYMMETRIC, "oppositeDirection" : true, "depth" : 25 * mm});
        }
        {
            var Q0;
            Q0=makeQuery(id+"F5.opExtrude","SWEPT_BODY",BODY,{"disambiguationData":[OSD([sQuery(id+"F2.wireOp",EDGE,"E20"),sQuery(id+"F2.wireOp",EDGE,"E21"),sQuery(id+"F2.wireOp",EDGE,"E22"),sQuery(id+"F2.wireOp",EDGE,"E23"),sQuery(id+"F2.wireOp",EDGE,"E24"),sQuery(id+"F2.wireOp",EDGE,"E25"),sQuery(id+"F2.wireOp",EDGE,"E171.filletArc"),sQuery(id+"F2.wireOp",EDGE,"E172.filletArc"),sQuery(id+"F2.wireOp",EDGE,"E173.filletArc"),sQuery(id+"F2.wireOp",EDGE,"E217.filletArc")])]});
            var Q1;
            Q1=makeQuery(id+"F5.opExtrude","SWEPT_BODY",BODY,{"disambiguationData":[OSD([sQuery(id+"F2.wireOp",EDGE,"E26"),sQuery(id+"F2.wireOp",EDGE,"E27"),sQuery(id+"F2.wireOp",EDGE,"E28"),sQuery(id+"F2.wireOp",EDGE,"E100"),sQuery(id+"F2.wireOp",EDGE,"E101"),sQuery(id+"F2.wireOp",EDGE,"E162.filletArc"),sQuery(id+"F2.wireOp",EDGE,"E163.filletArc"),sQuery(id+"F2.wireOp",EDGE,"E164.filletArc"),sQuery(id+"F2.wireOp",EDGE,"E165.filletArc"),sQuery(id+"F2.wireOp",EDGE,"E166.filletArc")])]});
            var Q2;
            Q2=makeQuery(id+"F5.opExtrude","SWEPT_BODY",BODY,{"disambiguationData":[OSD([sQuery(id+"F2.wireOp",EDGE,"E29"),sQuery(id+"F2.wireOp",EDGE,"E30"),sQuery(id+"F2.wireOp",EDGE,"E31"),sQuery(id+"F2.wireOp",EDGE,"E32"),sQuery(id+"F2.wireOp",EDGE,"E33"),sQuery(id+"F2.wireOp",EDGE,"E199.filletArc"),sQuery(id+"F2.wireOp",EDGE,"E200.filletArc"),sQuery(id+"F2.wireOp",EDGE,"E201.filletArc"),sQuery(id+"F2.wireOp",EDGE,"E202.filletArc"),sQuery(id+"F2.wireOp",EDGE,"E203.filletArc")])]});
            var Q3;
            Q3=makeQuery(id+"F5.opExtrude","SWEPT_BODY",BODY,{"disambiguationData":[OSD([sQuery(id+"F2.wireOp",EDGE,"E34"),sQuery(id+"F2.wireOp",EDGE,"E35"),sQuery(id+"F2.wireOp",EDGE,"E36"),sQuery(id+"F2.wireOp",EDGE,"E37"),sQuery(id+"F2.wireOp",EDGE,"E38"),sQuery(id+"F2.wireOp",EDGE,"E39"),sQuery(id+"F2.wireOp",EDGE,"E40"),sQuery(id+"F2.wireOp",EDGE,"E179.filletArc"),sQuery(id+"F2.wireOp",EDGE,"E180.filletArc"),sQuery(id+"F2.wireOp",EDGE,"E181.filletArc"),sQuery(id+"F2.wireOp",EDGE,"E182.filletArc"),sQuery(id+"F2.wireOp",EDGE,"E183.filletArc")])]});
            var Q4;
            Q4=makeQuery(id+"F5.opExtrude","SWEPT_BODY",BODY,{"disambiguationData":[OSD([sQuery(id+"F2.wireOp",EDGE,"E49"),sQuery(id+"F2.wireOp",EDGE,"E50"),sQuery(id+"F2.wireOp",EDGE,"E117"),sQuery(id+"F2.wireOp",EDGE,"E122.trimOffspring"),sQuery(id+"F2.wireOp",EDGE,"E189.filletArc"),sQuery(id+"F2.wireOp",EDGE,"E190.filletArc"),sQuery(id+"F2.wireOp",EDGE,"E192.filletArc"),sQuery(id+"F2.wireOp",EDGE,"E193.filletArc")])]});
            var Q5;
            Q5=makeQuery(id+"F5.opExtrude","SWEPT_BODY",BODY,{"disambiguationData":[OSD([sQuery(id+"F2.wireOp",EDGE,"E51"),sQuery(id+"F2.wireOp",EDGE,"E52"),sQuery(id+"F2.wireOp",EDGE,"E53"),sQuery(id+"F2.wireOp",EDGE,"E118"),sQuery(id+"F2.wireOp",EDGE,"E121.trimOffspring"),sQuery(id+"F2.wireOp",EDGE,"E194.filletArc"),sQuery(id+"F2.wireOp",EDGE,"E195.filletArc"),sQuery(id+"F2.wireOp",EDGE,"E196.filletArc"),sQuery(id+"F2.wireOp",EDGE,"E197.filletArc"),sQuery(id+"F2.wireOp",EDGE,"E198.filletArc")])]});
            var Q6;
            Q6=makeQuery(id+"F5.opExtrude","SWEPT_BODY",BODY,{"disambiguationData":[OSD([sQuery(id+"F2.wireOp",EDGE,"E60"),sQuery(id+"F2.wireOp",EDGE,"E61"),sQuery(id+"F2.wireOp",EDGE,"E62"),sQuery(id+"F2.wireOp",EDGE,"E63"),sQuery(id+"F2.wireOp",EDGE,"E64"),sQuery(id+"F2.wireOp",EDGE,"E158.filletArc"),sQuery(id+"F2.wireOp",EDGE,"E159.filletArc"),sQuery(id+"F2.wireOp",EDGE,"E160.filletArc"),sQuery(id+"F2.wireOp",EDGE,"E161.filletArc")])]});
            var Q7;
            Q7=makeQuery(id+"F5.opExtrude","SWEPT_BODY",BODY,{"disambiguationData":[OSD([sQuery(id+"F2.wireOp",EDGE,"E65"),sQuery(id+"F2.wireOp",EDGE,"E66"),sQuery(id+"F2.wireOp",EDGE,"E67"),sQuery(id+"F2.wireOp",EDGE,"E115"),sQuery(id+"F2.wireOp",EDGE,"E151.filletArc"),sQuery(id+"F2.wireOp",EDGE,"E152.filletArc"),sQuery(id+"F2.wireOp",EDGE,"E153.filletArc"),sQuery(id+"F2.wireOp",EDGE,"E156.filletArc")])]});
            var Q8;
            Q8=makeQuery(id+"F5.opExtrude","SWEPT_BODY",BODY,{"disambiguationData":[OSD([sQuery(id+"F2.wireOp",EDGE,"E73"),sQuery(id+"F2.wireOp",EDGE,"E74"),sQuery(id+"F2.wireOp",EDGE,"E75"),sQuery(id+"F2.wireOp",EDGE,"E76"),sQuery(id+"F2.wireOp",EDGE,"E136.filletArc"),sQuery(id+"F2.wireOp",EDGE,"E137.filletArc"),sQuery(id+"F2.wireOp",EDGE,"E138.filletArc"),sQuery(id+"F2.wireOp",EDGE,"E139.filletArc")])]});
            var Q9;
            Q9=makeQuery(id+"F5.opExtrude","SWEPT_BODY",BODY,{"disambiguationData":[OSD([sQuery(id+"F2.wireOp",EDGE,"E102"),sQuery(id+"F2.wireOp",EDGE,"E103"),sQuery(id+"F2.wireOp",EDGE,"E104"),sQuery(id+"F2.wireOp",EDGE,"E105"),sQuery(id+"F2.wireOp",EDGE,"E106"),sQuery(id+"F2.wireOp",EDGE,"E167.filletArc"),sQuery(id+"F2.wireOp",EDGE,"E168.filletArc"),sQuery(id+"F2.wireOp",EDGE,"E169.filletArc"),sQuery(id+"F2.wireOp",EDGE,"E170.filletArc"),sQuery(id+"F2.wireOp",EDGE,"E212.filletArc")])]});
            var Q10;
            Q10=makeQuery(id+"F5.opExtrude","SWEPT_BODY",BODY,{"disambiguationData":[OSD([sQuery(id+"F2.wireOp",EDGE,"E77"),sQuery(id+"F2.wireOp",EDGE,"E78"),sQuery(id+"F2.wireOp",EDGE,"E81"),sQuery(id+"F2.wireOp",EDGE,"E111"),sQuery(id+"F2.wireOp",EDGE,"E140.filletArc"),sQuery(id+"F2.wireOp",EDGE,"E141.filletArc"),sQuery(id+"F2.wireOp",EDGE,"E221.filletArc")])]});
            var Q11;
            Q11=makeQuery(id+"F5.opExtrude","SWEPT_BODY",BODY,{"disambiguationData":[OSD([sQuery(id+"F2.wireOp",EDGE,"E79"),sQuery(id+"F2.wireOp",EDGE,"E80"),sQuery(id+"F2.wireOp",EDGE,"E113.trimOffspring"),sQuery(id+"F2.wireOp",EDGE,"E133.filletArc"),sQuery(id+"F2.wireOp",EDGE,"E134.filletArc"),sQuery(id+"F2.wireOp",EDGE,"E135.filletArc"),sQuery(id+"F2.wireOp",EDGE,"E222"),sQuery(id+"F2.wireOp",EDGE,"E223.filletArc")])]});
            var Q12;
            Q12=makeQuery(id+"F5.opExtrude","SWEPT_BODY",BODY,{"disambiguationData":[OSD([sQuery(id+"F2.wireOp",EDGE,"E54"),sQuery(id+"F2.wireOp",EDGE,"E55"),sQuery(id+"F2.wireOp",EDGE,"E56"),sQuery(id+"F2.wireOp",EDGE,"E57"),sQuery(id+"F2.wireOp",EDGE,"E58"),sQuery(id+"F2.wireOp",EDGE,"E59"),sQuery(id+"F2.wireOp",EDGE,"E204.filletArc"),sQuery(id+"F2.wireOp",EDGE,"E205.filletArc"),sQuery(id+"F2.wireOp",EDGE,"E206.filletArc"),sQuery(id+"F2.wireOp",EDGE,"E207.filletArc")])]});
            var Q13;
            Q13=makeQuery(id+"F5.opExtrude","SWEPT_BODY",BODY,{"disambiguationData":[OSD([sQuery(id+"F2.wireOp",EDGE,"E70"),sQuery(id+"F2.wireOp",EDGE,"E71"),sQuery(id+"F2.wireOp",EDGE,"E72"),sQuery(id+"F2.wireOp",EDGE,"E154.filletArc"),sQuery(id+"F2.wireOp",EDGE,"E155.filletArc"),sQuery(id+"F2.wireOp",EDGE,"E157.filletArc")])]});
            var Q14;
            Q14=makeQuery(id+"F5.opExtrude","SWEPT_BODY",BODY,{"disambiguationData":[OSD([sQuery(id+"F2.wireOp",EDGE,"E68"),sQuery(id+"F2.wireOp",EDGE,"E69"),sQuery(id+"F2.wireOp",EDGE,"E114"),sQuery(id+"F2.wireOp",EDGE,"E116.trimOffspring"),sQuery(id+"F2.wireOp",EDGE,"E147.filletArc"),sQuery(id+"F2.wireOp",EDGE,"E148.filletArc"),sQuery(id+"F2.wireOp",EDGE,"E149.filletArc"),sQuery(id+"F2.wireOp",EDGE,"E150.filletArc")])]});
            var Q15;
            Q15=makeQuery(id+"F5.opExtrude","SWEPT_BODY",BODY,{"disambiguationData":[OSD([sQuery(id+"F2.wireOp",EDGE,"E107"),sQuery(id+"F2.wireOp",EDGE,"E108"),sQuery(id+"F2.wireOp",EDGE,"E109"),sQuery(id+"F2.wireOp",EDGE,"E110"),sQuery(id+"F2.wireOp",EDGE,"E208.filletArc"),sQuery(id+"F2.wireOp",EDGE,"E209.filletArc"),sQuery(id+"F2.wireOp",EDGE,"E210.filletArc"),sQuery(id+"F2.wireOp",EDGE,"E211.filletArc")])]});
            var Q16;
            Q16=makeQuery(id+"F5.opExtrude","SWEPT_BODY",BODY,{"disambiguationData":[OSD([sQuery(id+"F2.wireOp",EDGE,"E82"),sQuery(id+"F2.wireOp",EDGE,"E83"),sQuery(id+"F2.wireOp",EDGE,"E84"),sQuery(id+"F2.wireOp",EDGE,"E85"),sQuery(id+"F2.wireOp",EDGE,"E86"),sQuery(id+"F2.wireOp",EDGE,"E142.filletArc"),sQuery(id+"F2.wireOp",EDGE,"E143.filletArc"),sQuery(id+"F2.wireOp",EDGE,"E144.filletArc"),sQuery(id+"F2.wireOp",EDGE,"E145.filletArc"),sQuery(id+"F2.wireOp",EDGE,"E146.filletArc")])]});
            var Q17;
            Q17=makeQuery(id+"F5.opExtrude","SWEPT_BODY",BODY,{"disambiguationData":[OSD([sQuery(id+"F2.wireOp",EDGE,"E87"),sQuery(id+"F2.wireOp",EDGE,"E88"),sQuery(id+"F2.wireOp",EDGE,"E89"),sQuery(id+"F2.wireOp",EDGE,"E90"),sQuery(id+"F2.wireOp",EDGE,"E123.filletArc"),sQuery(id+"F2.wireOp",EDGE,"E218.filletArc"),sQuery(id+"F2.wireOp",EDGE,"E219.filletArc"),sQuery(id+"F2.wireOp",EDGE,"E220.filletArc")])]});
            var Q18;
            Q18=makeQuery(id+"F5.opExtrude","SWEPT_BODY",BODY,{"disambiguationData":[OSD([sQuery(id+"F2.wireOp",EDGE,"E91"),sQuery(id+"F2.wireOp",EDGE,"E92"),sQuery(id+"F2.wireOp",EDGE,"E93"),sQuery(id+"F2.wireOp",EDGE,"E94"),sQuery(id+"F2.wireOp",EDGE,"E124.filletArc"),sQuery(id+"F2.wireOp",EDGE,"E125.filletArc"),sQuery(id+"F2.wireOp",EDGE,"E126.filletArc"),sQuery(id+"F2.wireOp",EDGE,"E127.filletArc")])]});
            var Q19;
            Q19=makeQuery(id+"F5.opExtrude","SWEPT_BODY",BODY,{"disambiguationData":[OSD([sQuery(id+"F2.wireOp",EDGE,"E95"),sQuery(id+"F2.wireOp",EDGE,"E96"),sQuery(id+"F2.wireOp",EDGE,"E97"),sQuery(id+"F2.wireOp",EDGE,"E98"),sQuery(id+"F2.wireOp",EDGE,"E99"),sQuery(id+"F2.wireOp",EDGE,"E128.filletArc"),sQuery(id+"F2.wireOp",EDGE,"E129.filletArc"),sQuery(id+"F2.wireOp",EDGE,"E130.filletArc"),sQuery(id+"F2.wireOp",EDGE,"E131.filletArc"),sQuery(id+"F2.wireOp",EDGE,"E132.filletArc")])]});
            var Q20;
            Q20=makeQuery(id+"F5.opExtrude","SWEPT_BODY",BODY,{"disambiguationData":[OSD([sQuery(id+"F2.wireOp",EDGE,"E41"),sQuery(id+"F2.wireOp",EDGE,"E42"),sQuery(id+"F2.wireOp",EDGE,"E43"),sQuery(id+"F2.wireOp",EDGE,"E48"),sQuery(id+"F2.wireOp",EDGE,"E120"),sQuery(id+"F2.wireOp",EDGE,"E184.filletArc"),sQuery(id+"F2.wireOp",EDGE,"E185.filletArc"),sQuery(id+"F2.wireOp",EDGE,"E186.filletArc"),sQuery(id+"F2.wireOp",EDGE,"E213.filletArc"),sQuery(id+"F2.wireOp",EDGE,"E216.filletArc")])]});
            var Q21;
            Q21=makeQuery(id+"F5.opExtrude","SWEPT_BODY",BODY,{"disambiguationData":[OSD([sQuery(id+"F2.wireOp",EDGE,"E44"),sQuery(id+"F2.wireOp",EDGE,"E45"),sQuery(id+"F2.wireOp",EDGE,"E46"),sQuery(id+"F2.wireOp",EDGE,"E47"),sQuery(id+"F2.wireOp",EDGE,"E119"),sQuery(id+"F2.wireOp",EDGE,"E187.filletArc"),sQuery(id+"F2.wireOp",EDGE,"E188.filletArc"),sQuery(id+"F2.wireOp",EDGE,"E191.filletArc"),sQuery(id+"F2.wireOp",EDGE,"E214.filletArc"),sQuery(id+"F2.wireOp",EDGE,"E215.filletArc")])]});
            var Q22;
            Q22=makeQuery(id+"F5.opExtrude","SWEPT_BODY",BODY,{"disambiguationData":[OSD([sQuery(id+"F2.wireOp",EDGE,"E15"),sQuery(id+"F2.wireOp",EDGE,"E16"),sQuery(id+"F2.wireOp",EDGE,"E17"),sQuery(id+"F2.wireOp",EDGE,"E18"),sQuery(id+"F2.wireOp",EDGE,"E19"),sQuery(id+"F2.wireOp",EDGE,"E174.filletArc"),sQuery(id+"F2.wireOp",EDGE,"E175.filletArc"),sQuery(id+"F2.wireOp",EDGE,"E176.filletArc"),sQuery(id+"F2.wireOp",EDGE,"E177.filletArc"),sQuery(id+"F2.wireOp",EDGE,"E178.filletArc")])]});
            var Q23;
            Q23=makeQuery(id+"F4.opExtrude","SWEPT_BODY",BODY,{"disambiguationData":[OSD([sQuery(id+"F0.wireOp",EDGE,"E1"),sQuery(id+"F0.wireOp",EDGE,"E2"),sQuery(id+"F0.wireOp",EDGE,"E3"),sQuery(id+"F0.wireOp",EDGE,"E4")])]});
            booleanBodies(context, id + "F7", {"operationType" : BooleanOperationType.SUBTRACTION, "tools" : qUnion([Q0, Q1, Q2, Q3, Q4, Q5, Q6, Q7, Q8, Q9, Q10, Q11, Q12, Q13, Q14, Q15, Q16, Q17, Q18, Q19, Q20, Q21, Q22]), "targets" : qUnion([Q23])});
        }
        {
            var Q0;
            Q0=makeQuery(id+"F4.opExtrude","CAP_FACE",FACE,{"disambiguationData":[OSD([sQuery(id+"F0.wireOp",EDGE,"E1"),sQuery(id+"F0.wireOp",EDGE,"E2"),sQuery(id+"F0.wireOp",EDGE,"E3"),sQuery(id+"F0.wireOp",EDGE,"E4")])],"isStart":false});
            var sketch = newSketch(context, id + "F8", { "sketchPlane" : qUnion([Q0])});
            skLineSegment(sketch, "E494", {"start": v(30.8, 159.98) * mm, "end": v(31.02, 154.98) * mm});
            skLineSegment(sketch, "E495", {"start": v(31.02, 154.98) * mm, "end": v(28.52, 154.88) * mm});
            skLineSegment(sketch, "E496", {"start": v(28.52, 154.88) * mm, "end": v(28.69, 150.88) * mm});
            skLineSegment(sketch, "E497", {"start": v(28.69, 150.88) * mm, "end": v(31.19, 150.98) * mm});
            skLineSegment(sketch, "E498", {"start": v(31.19, 150.98) * mm, "end": v(34.13, 81.05) * mm});
            skLineSegment(sketch, "E499", {"start": v(34.13, 81.05) * mm, "end": v(31.63, 80.94) * mm});
            skLineSegment(sketch, "E500", {"start": v(31.63, 80.94) * mm, "end": v(31.8, 76.94) * mm});
            skLineSegment(sketch, "E501", {"start": v(31.8, 76.94) * mm, "end": v(34.3, 77.05) * mm});
            skLineSegment(sketch, "E502", {"start": v(34.3, 77.05) * mm, "end": v(34.13, 81.05) * mm});
            skLineSegment(sketch, "E503", {"start": v(31.02, 154.98) * mm, "end": v(31.19, 150.98) * mm});
            skLineSegment(sketch, "E504", {"start": v(34.3, 77.05) * mm, "end": v(37.24, 7.11) * mm});
            skLineSegment(sketch, "E505", {"start": v(37.24, 7.11) * mm, "end": v(34.74, 7) * mm});
            skLineSegment(sketch, "E506", {"start": v(34.74, 7) * mm, "end": v(34.9, 3) * mm});
            skLineSegment(sketch, "E507", {"start": v(34.9, 3) * mm, "end": v(37.4, 3.11) * mm});
            skLineSegment(sketch, "E508", {"start": v(37.4, 3.11) * mm, "end": v(37.24, 7.11) * mm});
            skLineSegment(sketch, "E509", {"start": v(30.8, 159.98) * mm, "end": v(15.8, 159.98) * mm});
            skLineSegment(sketch, "E510", {"start": v(15.8, 159.98) * mm, "end": v(15.8, 157.48) * mm});
            skLineSegment(sketch, "E511", {"start": v(15.8, 157.48) * mm, "end": v(11.8, 157.48) * mm});
            skLineSegment(sketch, "E512", {"start": v(11.8, 157.48) * mm, "end": v(11.8, 159.98) * mm});
            skLineSegment(sketch, "E513", {"start": v(11.8, 159.98) * mm, "end": v(15.8, 159.98) * mm});
            skLineSegment(sketch, "E514", {"start": v(11.8, 159.98) * mm, "end": v(-3.2, 159.98) * mm});
            skLineSegment(sketch, "E515", {"start": v(-3.2, 159.98) * mm, "end": v(-3.2, 157.48) * mm});
            skLineSegment(sketch, "E516", {"start": v(-3.2, 157.48) * mm, "end": v(-7.2, 157.48) * mm});
            skLineSegment(sketch, "E517", {"start": v(-7.2, 157.48) * mm, "end": v(-7.2, 159.98) * mm});
            skLineSegment(sketch, "E518", {"start": v(-7.2, 159.98) * mm, "end": v(-3.2, 159.98) * mm});
            skLineSegment(sketch, "E519", {"start": v(-7.2, 159.98) * mm, "end": v(-22.2, 159.98) * mm});
            skLineSegment(sketch, "E520", {"start": v(-22.2, 159.98) * mm, "end": v(-22.2, 157.48) * mm});
            skLineSegment(sketch, "E521", {"start": v(-22.2, 157.48) * mm, "end": v(-26.2, 157.48) * mm});
            skLineSegment(sketch, "E522", {"start": v(-26.2, 157.48) * mm, "end": v(-26.2, 159.98) * mm});
            skLineSegment(sketch, "E523", {"start": v(-26.2, 159.98) * mm, "end": v(-22.2, 159.98) * mm});
            skSolve(sketch);
        }
        {
            var Q0;
            Q0=makeQuery(id+"F4.opExtrude","CAP_FACE",FACE,{"disambiguationData":[OSD([sQuery(id+"F1.wireOp",EDGE,"E8"),sQuery(id+"F1.wireOp",EDGE,"E9"),sQuery(id+"F1.wireOp",EDGE,"E10"),sQuery(id+"F1.wireOp",EDGE,"E11")])],"isStart":false});
            var sketch = newSketch(context, id + "F9", { "sketchPlane" : qUnion([Q0])});
            skLineSegment(sketch, "E524", {"start": v(-115.37, 176.62) * mm, "end": v(-117.06, 171.9) * mm});
            skLineSegment(sketch, "E525", {"start": v(-117.06, 171.9) * mm, "end": v(-114.7, 171.07) * mm});
            skLineSegment(sketch, "E526", {"start": v(-114.7, 171.07) * mm, "end": v(-116.05, 167.3) * mm});
            skLineSegment(sketch, "E527", {"start": v(-116.05, 167.3) * mm, "end": v(-118.4, 168.14) * mm});
            skLineSegment(sketch, "E528", {"start": v(-118.4, 168.14) * mm, "end": v(-117.06, 171.9) * mm});
            skLineSegment(sketch, "E529", {"start": v(-118.4, 168.14) * mm, "end": v(-141.95, 102.22) * mm});
            skLineSegment(sketch, "E530", {"start": v(-141.95, 102.22) * mm, "end": v(-139.6, 101.38) * mm});
            skLineSegment(sketch, "E531", {"start": v(-139.6, 101.38) * mm, "end": v(-140.94, 97.61) * mm});
            skLineSegment(sketch, "E532", {"start": v(-140.94, 97.61) * mm, "end": v(-143.3, 98.46) * mm});
            skLineSegment(sketch, "E533", {"start": v(-143.3, 98.46) * mm, "end": v(-141.95, 102.22) * mm});
            skLineSegment(sketch, "E534", {"start": v(-143.3, 98.46) * mm, "end": v(-166.85, 32.54) * mm});
            skLineSegment(sketch, "E535", {"start": v(-166.85, 32.54) * mm, "end": v(-164.5, 31.7) * mm});
            skLineSegment(sketch, "E536", {"start": v(-164.5, 31.7) * mm, "end": v(-165.84, 27.93) * mm});
            skLineSegment(sketch, "E537", {"start": v(-165.84, 27.93) * mm, "end": v(-168.2, 28.77) * mm});
            skLineSegment(sketch, "E538", {"start": v(-168.2, 28.77) * mm, "end": v(-166.85, 32.54) * mm});
            skSolve(sketch);
        }
        {
            var Q0;
            Q0 = qSketchRegion(id + "F8", true);
            extrude(context, id + "F10", {"entities" : qUnion([Q0]), "operationType" : NewBodyOperationType.ADD, "depth" : 4 * mm});
        }
        {
            var Q0;
            Q0 = qSketchRegion(id + "F9", true);
            extrude(context, id + "F11", {"entities" : qUnion([Q0]), "operationType" : NewBodyOperationType.ADD, "depth" : 4 * mm});
        }
        {
            var Q0;
            Q0=makeQuery(id+"F10.boolean.opBoolean","MERGE",FACE,{"derivedFrom":[makeQuery(id+"F4.opExtrude","SWEPT_FACE",FACE,{"disambiguationData":[OSD([sQuery(id+"F0.wireOp",EDGE,"E1")])]}),makeQuery(id+"F10.opExtrude","SWEPT_FACE",FACE,{"disambiguationData":[OSD([sQuery(id+"F8.wireOp",EDGE,"E502")])]}),makeQuery(id+"F10.opExtrude","SWEPT_FACE",FACE,{"disambiguationData":[OSD([sQuery(id+"F8.wireOp",EDGE,"E503")])]}),makeQuery(id+"F10.opExtrude","SWEPT_FACE",FACE,{"disambiguationData":[OSD([sQuery(id+"F8.wireOp",EDGE,"E508")])]})]});
            var sketch = newSketch(context, id + "F12", { "sketchPlane" : qUnion([Q0])});
            skCircle(sketch, "E539", {"center": v(3.54, 5) * mm, "radius": 1.1 * mm});
            skPoint(sketch, "E539.centerSnap0", {"position": v(3.54, 7) * mm});
            skPoint(sketch, "E539.centerSnap1", {"position": v(1.54, 5) * mm});
            skCircle(sketch, "E540", {"center": v(77.54, 5) * mm, "radius": 1.1 * mm});
            skPoint(sketch, "E540.centerSnap0", {"position": v(77.54, 7) * mm});
            skCircle(sketch, "E541", {"center": v(151.54, 5) * mm, "radius": 1.1 * mm});
            skPoint(sketch, "E541.centerSnap0", {"position": v(151.54, 7) * mm});
            skSolve(sketch);
        }
        {
            var Q0;
            Q0 = qSketchRegion(id + "F12", true);
            extrude(context, id + "F13", {"entities" : qUnion([Q0]), "operationType" : NewBodyOperationType.REMOVE, "oppositeDirection" : true, "depth" : 25 * mm});
        }
        {
            var Q0;
            Q0=makeQuery(id+"F10.boolean.opBoolean","MERGE",FACE,{"derivedFrom":[makeQuery(id+"F4.opExtrude","SWEPT_FACE",FACE,{"disambiguationData":[OSD([sQuery(id+"F0.wireOp",EDGE,"E2")])]}),makeQuery(id+"F10.opExtrude","SWEPT_FACE",FACE,{"disambiguationData":[OSD([sQuery(id+"F8.wireOp",EDGE,"E513")])]}),makeQuery(id+"F10.opExtrude","SWEPT_FACE",FACE,{"disambiguationData":[OSD([sQuery(id+"F8.wireOp",EDGE,"E518")])]}),makeQuery(id+"F10.opExtrude","SWEPT_FACE",FACE,{"disambiguationData":[OSD([sQuery(id+"F8.wireOp",EDGE,"E523")])]})]});
            var sketch = newSketch(context, id + "F14", { "sketchPlane" : qUnion([Q0])});
            skCircle(sketch, "E542", {"center": v(-13.8, 5) * mm, "radius": 1.1 * mm});
            skPoint(sketch, "E542.centerSnap0", {"position": v(-13.8, 7) * mm});
            skPoint(sketch, "E542.centerSnap1", {"position": v(-11.8, 5) * mm});
            skCircle(sketch, "E543", {"center": v(5.2, 5) * mm, "radius": 1.1 * mm});
            skPoint(sketch, "E543.centerSnap0", {"position": v(3.2, 5) * mm});
            skPoint(sketch, "E543.centerSnap1", {"position": v(5.2, 7) * mm});
            skCircle(sketch, "E544", {"center": v(24.2, 5) * mm, "radius": 1.1 * mm});
            skPoint(sketch, "E544.centerSnap0", {"position": v(24.2, 7) * mm});
            skPoint(sketch, "E544.centerSnap1", {"position": v(22.2, 5) * mm});
            skSolve(sketch);
        }
        {
            var Q0;
            Q0 = qSketchRegion(id + "F14", true);
            extrude(context, id + "F15", {"entities" : qUnion([Q0]), "operationType" : NewBodyOperationType.REMOVE, "oppositeDirection" : true, "depth" : 25 * mm});
        }
        {
            var Q0;
            Q0=makeQuery(id+"F11.boolean.opBoolean","MERGE",FACE,{"derivedFrom":[makeQuery(id+"F4.opExtrude","SWEPT_FACE",FACE,{"disambiguationData":[OSD([sQuery(id+"F1.wireOp",EDGE,"E8")])]}),makeQuery(id+"F11.opExtrude","SWEPT_FACE",FACE,{"disambiguationData":[OSD([sQuery(id+"F9.wireOp",EDGE,"E528")])]}),makeQuery(id+"F11.opExtrude","SWEPT_FACE",FACE,{"disambiguationData":[OSD([sQuery(id+"F9.wireOp",EDGE,"E533")])]}),makeQuery(id+"F11.opExtrude","SWEPT_FACE",FACE,{"disambiguationData":[OSD([sQuery(id+"F9.wireOp",EDGE,"E538")])]})]});
            var sketch = newSketch(context, id + "F16", { "sketchPlane" : qUnion([Q0])});
            skCircle(sketch, "E545", {"center": v(-46.5, 5) * mm, "radius": 1.15 * mm});
            skPoint(sketch, "E545.centerSnap0", {"position": v(-48.5, 5) * mm});
            skPoint(sketch, "E545.centerSnap1", {"position": v(-46.5, 7) * mm});
            skCircle(sketch, "E546", {"center": v(27.5, 5) * mm, "radius": 1.15 * mm});
            skPoint(sketch, "E546.centerSnap0", {"position": v(27.5, 7) * mm});
            skCircle(sketch, "E547", {"center": v(-120.5, 5) * mm, "radius": 1.15 * mm});
            skPoint(sketch, "E547.centerSnap0", {"position": v(-120.5, 7) * mm});
            skSolve(sketch);
        }
        {
            var Q0;
            Q0 = qSketchRegion(id + "F16", true);
            extrude(context, id + "F17", {"entities" : qUnion([Q0]), "operationType" : NewBodyOperationType.REMOVE, "oppositeDirection" : true, "depth" : 25 * mm});
        }
        {
            var Q0;
            Q0=makeQuery(id+"F11.opExtrude","CAP_EDGE",EDGE,{"disambiguationData":[OSD([sQuery(id+"F9.wireOp",EDGE,"E530")])],"isStart":false});
            var Q1;
            Q1=makeQuery(id+"F11.opExtrude","CAP_EDGE",EDGE,{"disambiguationData":[OSD([sQuery(id+"F9.wireOp",EDGE,"E532")])],"isStart":false});
            var Q2;
            Q2=makeQuery(id+"F11.opExtrude","CAP_EDGE",EDGE,{"disambiguationData":[OSD([sQuery(id+"F9.wireOp",EDGE,"E537")])],"isStart":false});
            var Q3;
            Q3=makeQuery(id+"F11.opExtrude","CAP_EDGE",EDGE,{"disambiguationData":[OSD([sQuery(id+"F9.wireOp",EDGE,"E535")])],"isStart":false});
            var Q4;
            Q4=makeQuery(id+"F11.opExtrude","CAP_EDGE",EDGE,{"disambiguationData":[OSD([sQuery(id+"F9.wireOp",EDGE,"E527")])],"isStart":false});
            var Q5;
            Q5=makeQuery(id+"F11.opExtrude","CAP_EDGE",EDGE,{"disambiguationData":[OSD([sQuery(id+"F9.wireOp",EDGE,"E525")])],"isStart":false});
            var Q6;
            Q6=makeQuery(id+"F10.opExtrude","CAP_EDGE",EDGE,{"disambiguationData":[OSD([sQuery(id+"F8.wireOp",EDGE,"E522")])],"isStart":false});
            var Q7;
            Q7=makeQuery(id+"F10.opExtrude","CAP_EDGE",EDGE,{"disambiguationData":[OSD([sQuery(id+"F8.wireOp",EDGE,"E520")])],"isStart":false});
            var Q8;
            Q8=makeQuery(id+"F10.opExtrude","CAP_EDGE",EDGE,{"disambiguationData":[OSD([sQuery(id+"F8.wireOp",EDGE,"E517")])],"isStart":false});
            var Q9;
            Q9=makeQuery(id+"F10.opExtrude","CAP_EDGE",EDGE,{"disambiguationData":[OSD([sQuery(id+"F8.wireOp",EDGE,"E515")])],"isStart":false});
            var Q10;
            Q10=makeQuery(id+"F10.opExtrude","CAP_EDGE",EDGE,{"disambiguationData":[OSD([sQuery(id+"F8.wireOp",EDGE,"E512")])],"isStart":false});
            var Q11;
            Q11=makeQuery(id+"F10.opExtrude","CAP_EDGE",EDGE,{"disambiguationData":[OSD([sQuery(id+"F8.wireOp",EDGE,"E510")])],"isStart":false});
            var Q12;
            Q12=makeQuery(id+"F10.opExtrude","CAP_EDGE",EDGE,{"disambiguationData":[OSD([sQuery(id+"F8.wireOp",EDGE,"E495")])],"isStart":false});
            var Q13;
            Q13=makeQuery(id+"F10.opExtrude","CAP_EDGE",EDGE,{"disambiguationData":[OSD([sQuery(id+"F8.wireOp",EDGE,"E497")])],"isStart":false});
            var Q14;
            Q14=makeQuery(id+"F10.opExtrude","CAP_EDGE",EDGE,{"disambiguationData":[OSD([sQuery(id+"F8.wireOp",EDGE,"E499")])],"isStart":false});
            var Q15;
            Q15=makeQuery(id+"F10.opExtrude","CAP_EDGE",EDGE,{"disambiguationData":[OSD([sQuery(id+"F8.wireOp",EDGE,"E501")])],"isStart":false});
            var Q16;
            Q16=makeQuery(id+"F10.opExtrude","CAP_EDGE",EDGE,{"disambiguationData":[OSD([sQuery(id+"F8.wireOp",EDGE,"E505")])],"isStart":false});
            var Q17;
            Q17=makeQuery(id+"F10.opExtrude","CAP_EDGE",EDGE,{"disambiguationData":[OSD([sQuery(id+"F8.wireOp",EDGE,"E507")])],"isStart":false});
            fillet(context, id + "F18", {"entities" : qUnion([Q0, Q1, Q2, Q3, Q4, Q5, Q6, Q7, Q8, Q9, Q10, Q11, Q12, Q13, Q14, Q15, Q16, Q17]), "radius" : 1 * mm, "tangentPropagation" : true, "allowEdgeOverflow" : false});
        }
        {
            var Q0;
            Q0=makeQuery(id+"F4.opExtrude","CAP_EDGE",EDGE,{"disambiguationData":[OSD([sQuery(id+"F1.wireOp",EDGE,"E9")])],"isStart":true});
            var Q1;
            Q1=makeQuery(id+"F4.opExtrude","CAP_EDGE",EDGE,{"disambiguationData":[OSD([sQuery(id+"F0.wireOp",EDGE,"E3")])],"isStart":true});
            var Q2;
            Q2=makeQuery(id+"F4.opExtrude","CAP_EDGE",EDGE,{"disambiguationData":[OSD([sQuery(id+"F1.wireOp",EDGE,"E10")])],"isStart":true});
            var Q3;
            Q3=makeQuery(id+"F4.opExtrude","CAP_EDGE",EDGE,{"disambiguationData":[OSD([sQuery(id+"F1.wireOp",EDGE,"E10")])],"isStart":false});
            var Q4;
            Q4=makeQuery(id+"F4.opExtrude","CAP_EDGE",EDGE,{"disambiguationData":[OSD([sQuery(id+"F0.wireOp",EDGE,"E3")])],"isStart":false});
            fillet(context, id + "F19", {"entities" : qUnion([Q0, Q1, Q2, Q3, Q4]), "radius" : 1 * mm, "tangentPropagation" : true, "allowEdgeOverflow" : false});
        }
        {
            var Q0;
            Q0=makeQuery(id+"F7.opBoolean","INTERSECT",EDGE,{"derivedFrom":[makeQuery(id+"F4.opExtrude","CAP_FACE",FACE,{"disambiguationData":[OSD([sQuery(id+"F0.wireOp",EDGE,"E1"),sQuery(id+"F0.wireOp",EDGE,"E2"),sQuery(id+"F0.wireOp",EDGE,"E3"),sQuery(id+"F0.wireOp",EDGE,"E4"),sQuery(id+"F0.wireOp",EDGE,"E5.filletArc"),sQuery(id+"F0.wireOp",EDGE,"E6.filletArc"),sQuery(id+"F0.wireOp",EDGE,"E7.filletArc")])],"isStart":true}),makeQuery(id+"F5.opExtrude","SWEPT_FACE",FACE,{"disambiguationData":[OSD([sQuery(id+"F2.wireOp",EDGE,"E115")])]})]});
            var Q1;
            Q1=makeQuery(id+"F7.opBoolean","INTERSECT",EDGE,{"derivedFrom":[makeQuery(id+"F4.opExtrude","CAP_FACE",FACE,{"disambiguationData":[OSD([sQuery(id+"F0.wireOp",EDGE,"E1"),sQuery(id+"F0.wireOp",EDGE,"E2"),sQuery(id+"F0.wireOp",EDGE,"E3"),sQuery(id+"F0.wireOp",EDGE,"E4"),sQuery(id+"F0.wireOp",EDGE,"E5.filletArc"),sQuery(id+"F0.wireOp",EDGE,"E6.filletArc"),sQuery(id+"F0.wireOp",EDGE,"E7.filletArc")])],"isStart":true}),makeQuery(id+"F5.opExtrude","SWEPT_FACE",FACE,{"disambiguationData":[OSD([sQuery(id+"F2.wireOp",EDGE,"E57")])]})]});
            var Q2;
            Q2=makeQuery(id+"F7.opBoolean","INTERSECT",EDGE,{"derivedFrom":[makeQuery(id+"F4.opExtrude","CAP_FACE",FACE,{"disambiguationData":[OSD([sQuery(id+"F0.wireOp",EDGE,"E1"),sQuery(id+"F0.wireOp",EDGE,"E2"),sQuery(id+"F0.wireOp",EDGE,"E3"),sQuery(id+"F0.wireOp",EDGE,"E4"),sQuery(id+"F0.wireOp",EDGE,"E5.filletArc"),sQuery(id+"F0.wireOp",EDGE,"E6.filletArc"),sQuery(id+"F0.wireOp",EDGE,"E7.filletArc")])],"isStart":true}),makeQuery(id+"F5.opExtrude","SWEPT_FACE",FACE,{"disambiguationData":[OSD([sQuery(id+"F2.wireOp",EDGE,"E107")])]})]});
            var Q3;
            Q3=makeQuery(id+"F7.opBoolean","INTERSECT",EDGE,{"derivedFrom":[makeQuery(id+"F4.opExtrude","CAP_FACE",FACE,{"disambiguationData":[OSD([sQuery(id+"F0.wireOp",EDGE,"E1"),sQuery(id+"F0.wireOp",EDGE,"E2"),sQuery(id+"F0.wireOp",EDGE,"E3"),sQuery(id+"F0.wireOp",EDGE,"E4"),sQuery(id+"F0.wireOp",EDGE,"E5.filletArc"),sQuery(id+"F0.wireOp",EDGE,"E6.filletArc"),sQuery(id+"F0.wireOp",EDGE,"E7.filletArc")])],"isStart":true}),makeQuery(id+"F5.opExtrude","SWEPT_FACE",FACE,{"disambiguationData":[OSD([sQuery(id+"F2.wireOp",EDGE,"E31")])]})]});
            var Q4;
            Q4=makeQuery(id+"F7.opBoolean","INTERSECT",EDGE,{"derivedFrom":[makeQuery(id+"F4.opExtrude","CAP_FACE",FACE,{"disambiguationData":[OSD([sQuery(id+"F0.wireOp",EDGE,"E1"),sQuery(id+"F0.wireOp",EDGE,"E2"),sQuery(id+"F0.wireOp",EDGE,"E3"),sQuery(id+"F0.wireOp",EDGE,"E4"),sQuery(id+"F0.wireOp",EDGE,"E5.filletArc"),sQuery(id+"F0.wireOp",EDGE,"E6.filletArc"),sQuery(id+"F0.wireOp",EDGE,"E7.filletArc")])],"isStart":true}),makeQuery(id+"F5.opExtrude","SWEPT_FACE",FACE,{"disambiguationData":[OSD([sQuery(id+"F2.wireOp",EDGE,"E52")])]})]});
            var Q5;
            Q5=makeQuery(id+"F7.opBoolean","INTERSECT",EDGE,{"derivedFrom":[makeQuery(id+"F4.opExtrude","CAP_FACE",FACE,{"disambiguationData":[OSD([sQuery(id+"F0.wireOp",EDGE,"E1"),sQuery(id+"F0.wireOp",EDGE,"E2"),sQuery(id+"F0.wireOp",EDGE,"E3"),sQuery(id+"F0.wireOp",EDGE,"E4"),sQuery(id+"F0.wireOp",EDGE,"E5.filletArc"),sQuery(id+"F0.wireOp",EDGE,"E6.filletArc"),sQuery(id+"F0.wireOp",EDGE,"E7.filletArc")])],"isStart":true}),makeQuery(id+"F5.opExtrude","SWEPT_FACE",FACE,{"disambiguationData":[OSD([sQuery(id+"F2.wireOp",EDGE,"E117")])]})]});
            var Q6;
            Q6=makeQuery(id+"F7.opBoolean","INTERSECT",EDGE,{"derivedFrom":[makeQuery(id+"F4.opExtrude","CAP_FACE",FACE,{"disambiguationData":[OSD([sQuery(id+"F0.wireOp",EDGE,"E1"),sQuery(id+"F0.wireOp",EDGE,"E2"),sQuery(id+"F0.wireOp",EDGE,"E3"),sQuery(id+"F0.wireOp",EDGE,"E4"),sQuery(id+"F0.wireOp",EDGE,"E5.filletArc"),sQuery(id+"F0.wireOp",EDGE,"E6.filletArc"),sQuery(id+"F0.wireOp",EDGE,"E7.filletArc")])],"isStart":true}),makeQuery(id+"F5.opExtrude","SWEPT_FACE",FACE,{"disambiguationData":[OSD([sQuery(id+"F2.wireOp",EDGE,"E45")])]})]});
            var Q7;
            Q7=makeQuery(id+"F7.opBoolean","INTERSECT",EDGE,{"derivedFrom":[makeQuery(id+"F4.opExtrude","CAP_FACE",FACE,{"disambiguationData":[OSD([sQuery(id+"F0.wireOp",EDGE,"E1"),sQuery(id+"F0.wireOp",EDGE,"E2"),sQuery(id+"F0.wireOp",EDGE,"E3"),sQuery(id+"F0.wireOp",EDGE,"E4"),sQuery(id+"F0.wireOp",EDGE,"E5.filletArc"),sQuery(id+"F0.wireOp",EDGE,"E6.filletArc"),sQuery(id+"F0.wireOp",EDGE,"E7.filletArc")])],"isStart":true}),makeQuery(id+"F5.opExtrude","SWEPT_FACE",FACE,{"disambiguationData":[OSD([sQuery(id+"F2.wireOp",EDGE,"E120")])]})]});
            var Q8;
            Q8=makeQuery(id+"F7.opBoolean","INTERSECT",EDGE,{"derivedFrom":[makeQuery(id+"F4.opExtrude","CAP_FACE",FACE,{"disambiguationData":[OSD([sQuery(id+"F0.wireOp",EDGE,"E1"),sQuery(id+"F0.wireOp",EDGE,"E2"),sQuery(id+"F0.wireOp",EDGE,"E3"),sQuery(id+"F0.wireOp",EDGE,"E4"),sQuery(id+"F0.wireOp",EDGE,"E5.filletArc"),sQuery(id+"F0.wireOp",EDGE,"E6.filletArc"),sQuery(id+"F0.wireOp",EDGE,"E7.filletArc")])],"isStart":true}),makeQuery(id+"F5.opExtrude","SWEPT_FACE",FACE,{"disambiguationData":[OSD([sQuery(id+"F2.wireOp",EDGE,"E34")])]})]});
            var Q9;
            Q9=makeQuery(id+"F7.opBoolean","INTERSECT",EDGE,{"derivedFrom":[makeQuery(id+"F4.opExtrude","CAP_FACE",FACE,{"disambiguationData":[OSD([sQuery(id+"F0.wireOp",EDGE,"E1"),sQuery(id+"F0.wireOp",EDGE,"E2"),sQuery(id+"F0.wireOp",EDGE,"E3"),sQuery(id+"F0.wireOp",EDGE,"E4"),sQuery(id+"F0.wireOp",EDGE,"E5.filletArc"),sQuery(id+"F0.wireOp",EDGE,"E6.filletArc"),sQuery(id+"F0.wireOp",EDGE,"E7.filletArc")])],"isStart":true}),makeQuery(id+"F5.opExtrude","SWEPT_FACE",FACE,{"disambiguationData":[OSD([sQuery(id+"F2.wireOp",EDGE,"E25")])]})]});
            var Q10;
            Q10=makeQuery(id+"F7.opBoolean","INTERSECT",EDGE,{"derivedFrom":[makeQuery(id+"F4.opExtrude","CAP_FACE",FACE,{"disambiguationData":[OSD([sQuery(id+"F0.wireOp",EDGE,"E1"),sQuery(id+"F0.wireOp",EDGE,"E2"),sQuery(id+"F0.wireOp",EDGE,"E3"),sQuery(id+"F0.wireOp",EDGE,"E4"),sQuery(id+"F0.wireOp",EDGE,"E5.filletArc"),sQuery(id+"F0.wireOp",EDGE,"E6.filletArc"),sQuery(id+"F0.wireOp",EDGE,"E7.filletArc")])],"isStart":false}),makeQuery(id+"F5.opExtrude","SWEPT_FACE",FACE,{"disambiguationData":[OSD([sQuery(id+"F2.wireOp",EDGE,"E116.trimOffspring")])]})]});
            var Q11;
            Q11=makeQuery(id+"F7.opBoolean","INTERSECT",EDGE,{"derivedFrom":[makeQuery(id+"F4.opExtrude","CAP_FACE",FACE,{"disambiguationData":[OSD([sQuery(id+"F0.wireOp",EDGE,"E1"),sQuery(id+"F0.wireOp",EDGE,"E2"),sQuery(id+"F0.wireOp",EDGE,"E3"),sQuery(id+"F0.wireOp",EDGE,"E4"),sQuery(id+"F0.wireOp",EDGE,"E5.filletArc"),sQuery(id+"F0.wireOp",EDGE,"E6.filletArc"),sQuery(id+"F0.wireOp",EDGE,"E7.filletArc")])],"isStart":true}),makeQuery(id+"F5.opExtrude","SWEPT_FACE",FACE,{"disambiguationData":[OSD([sQuery(id+"F2.wireOp",EDGE,"E72")])]})]});
            var Q12;
            Q12=makeQuery(id+"F7.opBoolean","INTERSECT",EDGE,{"derivedFrom":[makeQuery(id+"F4.opExtrude","CAP_FACE",FACE,{"disambiguationData":[OSD([sQuery(id+"F0.wireOp",EDGE,"E1"),sQuery(id+"F0.wireOp",EDGE,"E2"),sQuery(id+"F0.wireOp",EDGE,"E3"),sQuery(id+"F0.wireOp",EDGE,"E4"),sQuery(id+"F0.wireOp",EDGE,"E5.filletArc"),sQuery(id+"F0.wireOp",EDGE,"E6.filletArc"),sQuery(id+"F0.wireOp",EDGE,"E7.filletArc")])],"isStart":true}),makeQuery(id+"F5.opExtrude","SWEPT_FACE",FACE,{"disambiguationData":[OSD([sQuery(id+"F2.wireOp",EDGE,"E101")])]})]});
            var Q13;
            Q13=makeQuery(id+"F7.opBoolean","INTERSECT",EDGE,{"derivedFrom":[makeQuery(id+"F4.opExtrude","CAP_FACE",FACE,{"disambiguationData":[OSD([sQuery(id+"F0.wireOp",EDGE,"E1"),sQuery(id+"F0.wireOp",EDGE,"E2"),sQuery(id+"F0.wireOp",EDGE,"E3"),sQuery(id+"F0.wireOp",EDGE,"E4"),sQuery(id+"F0.wireOp",EDGE,"E5.filletArc"),sQuery(id+"F0.wireOp",EDGE,"E6.filletArc"),sQuery(id+"F0.wireOp",EDGE,"E7.filletArc")])],"isStart":true}),makeQuery(id+"F5.opExtrude","SWEPT_FACE",FACE,{"disambiguationData":[OSD([sQuery(id+"F2.wireOp",EDGE,"E104")])]})]});
            var Q14;
            Q14=makeQuery(id+"F7.opBoolean","INTERSECT",EDGE,{"derivedFrom":[makeQuery(id+"F4.opExtrude","CAP_FACE",FACE,{"disambiguationData":[OSD([sQuery(id+"F0.wireOp",EDGE,"E1"),sQuery(id+"F0.wireOp",EDGE,"E2"),sQuery(id+"F0.wireOp",EDGE,"E3"),sQuery(id+"F0.wireOp",EDGE,"E4"),sQuery(id+"F0.wireOp",EDGE,"E5.filletArc"),sQuery(id+"F0.wireOp",EDGE,"E6.filletArc"),sQuery(id+"F0.wireOp",EDGE,"E7.filletArc")])],"isStart":true}),makeQuery(id+"F5.opExtrude","SWEPT_FACE",FACE,{"disambiguationData":[OSD([sQuery(id+"F2.wireOp",EDGE,"E18")])]})]});
            var Q15;
            Q15=makeQuery(id+"F7.opBoolean","INTERSECT",EDGE,{"derivedFrom":[makeQuery(id+"F4.opExtrude","CAP_FACE",FACE,{"disambiguationData":[OSD([sQuery(id+"F0.wireOp",EDGE,"E1"),sQuery(id+"F0.wireOp",EDGE,"E2"),sQuery(id+"F0.wireOp",EDGE,"E3"),sQuery(id+"F0.wireOp",EDGE,"E4"),sQuery(id+"F0.wireOp",EDGE,"E5.filletArc"),sQuery(id+"F0.wireOp",EDGE,"E6.filletArc"),sQuery(id+"F0.wireOp",EDGE,"E7.filletArc")])],"isStart":true}),makeQuery(id+"F5.opExtrude","SWEPT_FACE",FACE,{"disambiguationData":[OSD([sQuery(id+"F2.wireOp",EDGE,"E60")])]})]});
            var Q16;
            Q16=makeQuery(id+"F7.opBoolean","INTERSECT",EDGE,{"derivedFrom":[makeQuery(id+"F4.opExtrude","CAP_FACE",FACE,{"disambiguationData":[OSD([sQuery(id+"F0.wireOp",EDGE,"E1"),sQuery(id+"F0.wireOp",EDGE,"E2"),sQuery(id+"F0.wireOp",EDGE,"E3"),sQuery(id+"F0.wireOp",EDGE,"E4"),sQuery(id+"F0.wireOp",EDGE,"E5.filletArc"),sQuery(id+"F0.wireOp",EDGE,"E6.filletArc"),sQuery(id+"F0.wireOp",EDGE,"E7.filletArc")])],"isStart":true}),makeQuery(id+"F5.opExtrude","SWEPT_FACE",FACE,{"disambiguationData":[OSD([sQuery(id+"F2.wireOp",EDGE,"E73")])]})]});
            var Q17;
            Q17=makeQuery(id+"F7.opBoolean","INTERSECT",EDGE,{"derivedFrom":[makeQuery(id+"F4.opExtrude","CAP_FACE",FACE,{"disambiguationData":[OSD([sQuery(id+"F0.wireOp",EDGE,"E1"),sQuery(id+"F0.wireOp",EDGE,"E2"),sQuery(id+"F0.wireOp",EDGE,"E3"),sQuery(id+"F0.wireOp",EDGE,"E4"),sQuery(id+"F0.wireOp",EDGE,"E5.filletArc"),sQuery(id+"F0.wireOp",EDGE,"E6.filletArc"),sQuery(id+"F0.wireOp",EDGE,"E7.filletArc")])],"isStart":true}),makeQuery(id+"F5.opExtrude","SWEPT_FACE",FACE,{"disambiguationData":[OSD([sQuery(id+"F2.wireOp",EDGE,"E78")])]})]});
            var Q18;
            Q18=makeQuery(id+"F7.opBoolean","INTERSECT",EDGE,{"derivedFrom":[makeQuery(id+"F4.opExtrude","CAP_FACE",FACE,{"disambiguationData":[OSD([sQuery(id+"F0.wireOp",EDGE,"E1"),sQuery(id+"F0.wireOp",EDGE,"E2"),sQuery(id+"F0.wireOp",EDGE,"E3"),sQuery(id+"F0.wireOp",EDGE,"E4"),sQuery(id+"F0.wireOp",EDGE,"E5.filletArc"),sQuery(id+"F0.wireOp",EDGE,"E6.filletArc"),sQuery(id+"F0.wireOp",EDGE,"E7.filletArc")])],"isStart":true}),makeQuery(id+"F5.opExtrude","SWEPT_FACE",FACE,{"disambiguationData":[OSD([sQuery(id+"F2.wireOp",EDGE,"E223.filletArc")])]})]});
            var Q19;
            Q19=makeQuery(id+"F4.opExtrude","CAP_FACE",FACE,{"disambiguationData":[OSD([sQuery(id+"F0.wireOp",EDGE,"E1"),sQuery(id+"F0.wireOp",EDGE,"E2"),sQuery(id+"F0.wireOp",EDGE,"E3"),sQuery(id+"F0.wireOp",EDGE,"E4"),sQuery(id+"F0.wireOp",EDGE,"E5.filletArc"),sQuery(id+"F0.wireOp",EDGE,"E6.filletArc"),sQuery(id+"F0.wireOp",EDGE,"E7.filletArc")])],"isStart":true});
            fillet(context, id + "F20", {"entities" : qUnion([Q0, Q1, Q2, Q3, Q4, Q5, Q6, Q7, Q8, Q9, Q10, Q11, Q12, Q13, Q14, Q15, Q16, Q17, Q18, Q19]), "radius" : 1 * mm, "tangentPropagation" : true, "allowEdgeOverflow" : false});
        }
        {
            var Q0;
            Q0=makeQuery(id+"F4.opExtrude","CAP_FACE",FACE,{"disambiguationData":[OSD([sQuery(id+"F1.wireOp",EDGE,"E8"),sQuery(id+"F1.wireOp",EDGE,"E9"),sQuery(id+"F1.wireOp",EDGE,"E10"),sQuery(id+"F1.wireOp",EDGE,"E11"),sQuery(id+"F1.wireOp",EDGE,"E12.filletArc"),sQuery(id+"F1.wireOp",EDGE,"E13.filletArc"),sQuery(id+"F1.wireOp",EDGE,"E14.filletArc")])],"isStart":true});
            fillet(context, id + "F21", {"entities" : qUnion([Q0]), "radius" : 1 * mm, "tangentPropagation" : true, "allowEdgeOverflow" : false});
        }
        {
            var Q0;
            Q0=makeQuery(id+"F4.opExtrude","CAP_FACE",FACE,{"disambiguationData":[OSD([sQuery(id+"F0.wireOp",EDGE,"E1"),sQuery(id+"F0.wireOp",EDGE,"E2"),sQuery(id+"F0.wireOp",EDGE,"E3"),sQuery(id+"F0.wireOp",EDGE,"E4"),sQuery(id+"F0.wireOp",EDGE,"E5.filletArc"),sQuery(id+"F0.wireOp",EDGE,"E6.filletArc"),sQuery(id+"F0.wireOp",EDGE,"E7.filletArc")])],"isStart":false});
            var Q1;
            Q1=makeQuery(id+"F4.opExtrude","CAP_FACE",FACE,{"disambiguationData":[OSD([sQuery(id+"F1.wireOp",EDGE,"E8"),sQuery(id+"F1.wireOp",EDGE,"E9"),sQuery(id+"F1.wireOp",EDGE,"E10"),sQuery(id+"F1.wireOp",EDGE,"E11"),sQuery(id+"F1.wireOp",EDGE,"E12.filletArc"),sQuery(id+"F1.wireOp",EDGE,"E13.filletArc"),sQuery(id+"F1.wireOp",EDGE,"E14.filletArc")])],"isStart":false});
            fillet(context, id + "F22", {"entities" : qUnion([Q0, Q1]), "radius" : 1 * mm, "tangentPropagation" : true, "allowEdgeOverflow" : false});
        }
    });
